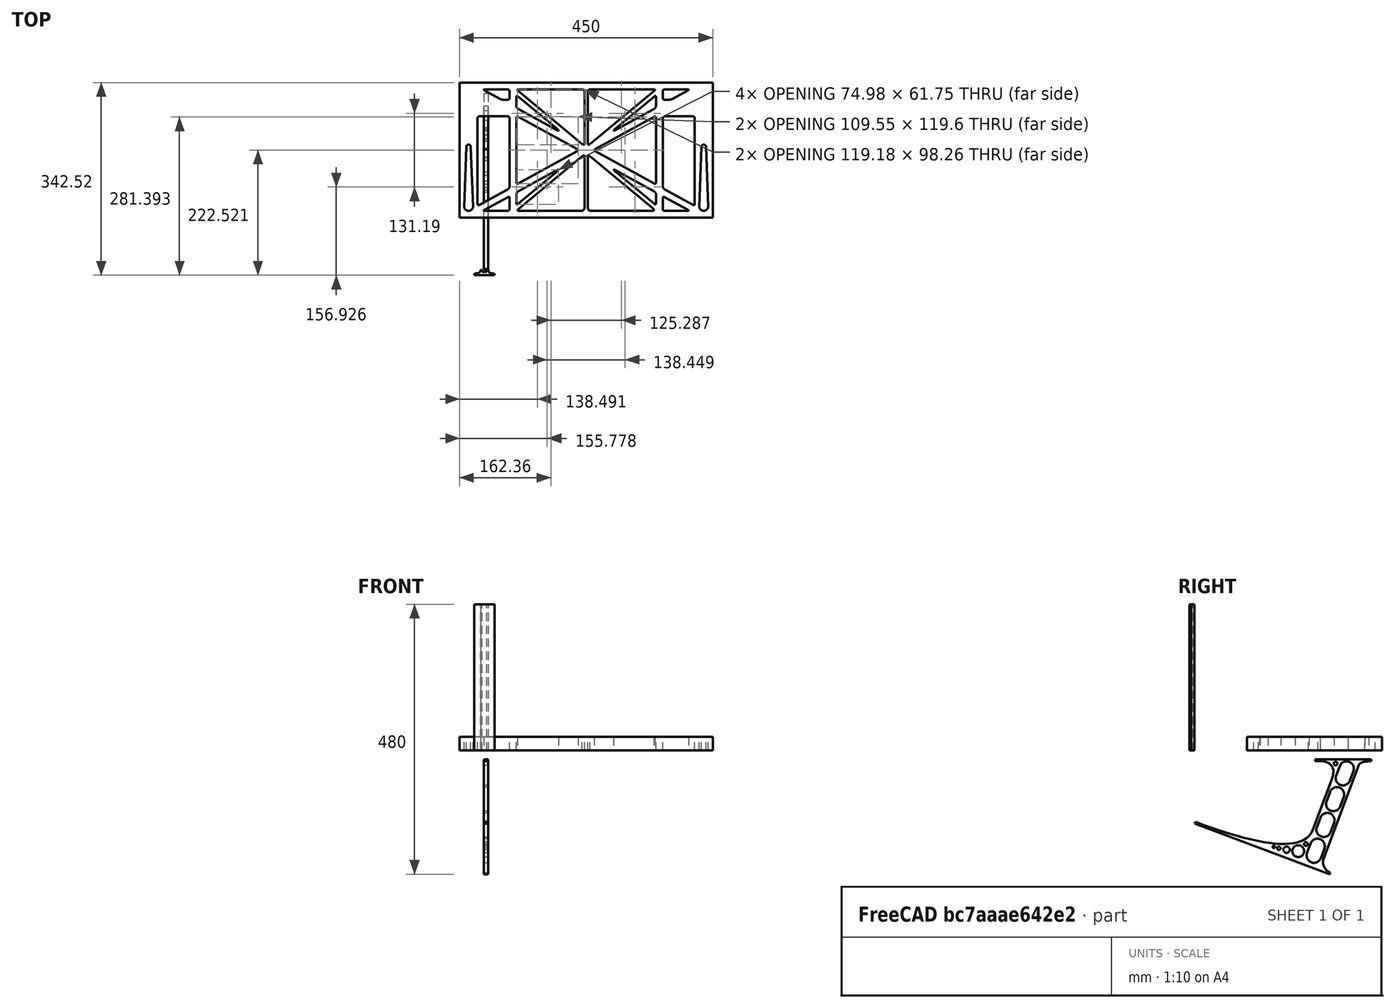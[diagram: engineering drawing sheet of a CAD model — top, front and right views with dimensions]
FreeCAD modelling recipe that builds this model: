
FCSTD DOCUMENT  (FreeCAD 0.19R0.19.2)
Label: laptopStand174FCStd
License: All rights reserved
LicenseURL: http://en.wikipedia.org/wiki/All_rights_reserved
objects: Sketcher::SketchObject×4, Part::Extrusion×3
note: 7 computed .brp shape members not serialized (recipe doc carries the construction recipe); baked Part::Feature solids carry a one-line shape summary decoded from their .brp

FEATURE [Sketcher::SketchObject] Sketch
  FullyConstrained = false
  sketch-geometry (349):
    g0: LineSegment StartX=-10.9272 StartY=-82.7794 StartZ=0 EndX=46.0728 EndY=-51.4823 EndZ=0
    g1: LineSegment StartX=-10.9272 StartY=76.4095 StartZ=0 EndX=-10.9272 EndY=-82.7794 EndZ=0
    g2: LineSegment StartX=46.0728 StartY=76.4095 StartZ=0 EndX=46.0728 EndY=-51.4823 EndZ=0
    g3: LineSegment StartX=-42.9272 StartY=136.221 StartZ=0 EndX=-42.9272 EndY=-103.779 EndZ=0
    g4: LineSegment StartX=407.073 StartY=136.221 StartZ=0 EndX=407.073 EndY=-103.779 EndZ=0
    g5: ArcOfCircle CenterX=-26.9272 CenterY=-83.7794 CenterZ=0 NormalX=0 NormalY=0 NormalZ=1 AngleXU=0 Radius=8 StartAngle=3.14159 EndAngle=6.28319
    g6: ArcOfCircle CenterX=391.073 CenterY=22.1087 CenterZ=0 NormalX=0 NormalY=0 NormalZ=1 AngleXU=0 Radius=8 StartAngle=-4.4e-15 EndAngle=3.14159
    g7: LineSegment StartX=399.073 StartY=22.1087 StartZ=0 EndX=399.073 EndY=-83.7794 EndZ=0
    g8: LineSegment StartX=383.073 StartY=22.1087 StartZ=0 EndX=383.073 EndY=-83.7794 EndZ=0
    g9: ArcOfCircle CenterX=391.073 CenterY=-83.7794 CenterZ=0 NormalX=0 NormalY=0 NormalZ=1 AngleXU=0 Radius=8 StartAngle=3.14159 EndAngle=6.28319
    g10: Circle CenterX=175.022 CenterY=27.0628 CenterZ=0 NormalX=0 NormalY=0 NormalZ=1 AngleXU=0 Radius=1
    g11: Circle CenterX=179.022 CenterY=24.8665 CenterZ=0 NormalX=0 NormalY=0 NormalZ=1 AngleXU=0 Radius=1
    g12: Circle CenterX=179.022 CenterY=27.0628 CenterZ=0 NormalX=0 NormalY=0 NormalZ=1 AngleXU=0 Radius=1
    g13: BSplineCurve PolesCount=3 KnotsCount=2 Degree=2 IsPeriodic=0
    g14: GeomPoint X=175.022 Y=27.0628 Z=0
    g15: GeomPoint X=179.022 Y=27.0628 Z=0
    g16: Circle CenterX=189.124 CenterY=27.0628 CenterZ=0 NormalX=0 NormalY=0 NormalZ=1 AngleXU=0 Radius=1
    g17: Circle CenterX=185.124 CenterY=24.8665 CenterZ=0 NormalX=0 NormalY=0 NormalZ=1 AngleXU=0 Radius=1
    g18: Circle CenterX=185.124 CenterY=27.0628 CenterZ=0 NormalX=0 NormalY=0 NormalZ=1 AngleXU=0 Radius=1
    g19: BSplineCurve PolesCount=3 KnotsCount=2 Degree=2 IsPeriodic=0
    g20: GeomPoint X=189.124 Y=27.0628 Z=0
    g21: GeomPoint X=185.124 Y=27.0628 Z=0
    g22: Circle CenterX=175.022 CenterY=5.37834 CenterZ=0 NormalX=0 NormalY=0 NormalZ=1 AngleXU=0 Radius=1
    g23: Circle CenterX=179.022 CenterY=7.57463 CenterZ=0 NormalX=0 NormalY=0 NormalZ=1 AngleXU=0 Radius=1
    g24: Circle CenterX=179.022 CenterY=5.34704 CenterZ=0 NormalX=0 NormalY=0 NormalZ=1 AngleXU=0 Radius=1
    g25: BSplineCurve PolesCount=3 KnotsCount=2 Degree=2 IsPeriodic=0
    g26: GeomPoint X=175.022 Y=5.37834 Z=0
    g27: GeomPoint X=179.022 Y=5.34704 Z=0
    g28: Circle CenterX=189.124 CenterY=5.37834 CenterZ=0 NormalX=0 NormalY=0 NormalZ=1 AngleXU=0 Radius=1
    g29: Circle CenterX=185.124 CenterY=7.57463 CenterZ=0 NormalX=0 NormalY=0 NormalZ=1 AngleXU=0 Radius=1
    g30: Circle CenterX=185.124 CenterY=5.34704 CenterZ=0 NormalX=0 NormalY=0 NormalZ=1 AngleXU=0 Radius=1
    g31: BSplineCurve PolesCount=3 KnotsCount=2 Degree=2 IsPeriodic=0
    g32: GeomPoint X=189.124 Y=5.37834 Z=0
    g33: GeomPoint X=185.124 Y=5.34704 Z=0
    g34: Circle CenterX=165.871 CenterY=18.1458 CenterZ=0 NormalX=0 NormalY=0 NormalZ=1 AngleXU=0 Radius=1
    g35: Circle CenterX=169.377 CenterY=16.2206 CenterZ=0 NormalX=0 NormalY=0 NormalZ=1 AngleXU=0 Radius=1
    g36: Circle CenterX=165.871 CenterY=14.2954 CenterZ=0 NormalX=0 NormalY=0 NormalZ=1 AngleXU=0 Radius=1
    g37: BSplineCurve PolesCount=3 KnotsCount=2 Degree=2 IsPeriodic=0
    g38: GeomPoint X=165.871 Y=18.1458 Z=0
    g39: GeomPoint X=165.871 Y=14.2954 Z=0
    g40: Circle CenterX=198.275 CenterY=18.1458 CenterZ=0 NormalX=0 NormalY=0 NormalZ=1 AngleXU=0 Radius=1
    g41: Circle CenterX=194.768 CenterY=16.2206 CenterZ=0 NormalX=0 NormalY=0 NormalZ=1 AngleXU=0 Radius=1
    g42: Circle CenterX=198.275 CenterY=14.2954 CenterZ=0 NormalX=0 NormalY=0 NormalZ=1 AngleXU=0 Radius=1
    g43: BSplineCurve PolesCount=3 KnotsCount=2 Degree=2 IsPeriodic=0
    g44: GeomPoint X=198.275 Y=18.1458 Z=0
    g45: GeomPoint X=198.275 Y=14.2954 Z=0
    g46: LineSegment StartX=407.073 StartY=-103.779 StartZ=0 EndX=-42.9272 EndY=-103.779 EndZ=0
    g47: LineSegment StartX=407.073 StartY=136.221 StartZ=0 EndX=-42.9272 EndY=136.221 EndZ=0
    g48: LineSegment StartX=46.0728 StartY=76.4095 StartZ=0 EndX=-10.9272 EndY=76.4095 EndZ=0
    g49: Circle CenterX=125.607 CenterY=54.1951 CenterZ=0 NormalX=0 NormalY=0 NormalZ=1 AngleXU=0 Radius=1
    g50: Circle CenterX=139.632 CenterY=46.4944 CenterZ=0 NormalX=0 NormalY=0 NormalZ=1 AngleXU=0 Radius=1
    g51: Circle CenterX=127.326 CenterY=56.7187 CenterZ=0 NormalX=0 NormalY=0 NormalZ=1 AngleXU=0 Radius=1
    g52: BSplineCurve PolesCount=3 KnotsCount=2 Degree=2 IsPeriodic=0
    g53: GeomPoint X=125.607 Y=54.1951 Z=0
    g54: GeomPoint X=127.326 Y=56.7187 Z=0
    g55: Circle CenterX=236.821 CenterY=56.7187 CenterZ=0 NormalX=0 NormalY=0 NormalZ=1 AngleXU=0 Radius=1
    g56: Circle CenterX=224.513 CenterY=46.4944 CenterZ=0 NormalX=0 NormalY=0 NormalZ=1 AngleXU=0 Radius=1
    g57: Circle CenterX=238.538 CenterY=54.1951 CenterZ=0 NormalX=0 NormalY=0 NormalZ=1 AngleXU=0 Radius=1
    g58: BSplineCurve PolesCount=3 KnotsCount=2 Degree=2 IsPeriodic=0
    g59: GeomPoint X=236.821 Y=56.7187 Z=0
    g60: GeomPoint X=238.538 Y=54.1951 Z=0
    g61: Circle CenterX=238.538 CenterY=-21.7539 CenterZ=0 NormalX=0 NormalY=0 NormalZ=1 AngleXU=0 Radius=1
    g62: Circle CenterX=224.513 CenterY=-14.0532 CenterZ=0 NormalX=0 NormalY=0 NormalZ=1 AngleXU=0 Radius=1
    g63: Circle CenterX=236.821 CenterY=-24.2775 CenterZ=0 NormalX=0 NormalY=0 NormalZ=1 AngleXU=0 Radius=1
    g64: BSplineCurve PolesCount=3 KnotsCount=2 Degree=2 IsPeriodic=0
    g65: GeomPoint X=238.538 Y=-21.7539 Z=0
    g66: GeomPoint X=236.821 Y=-24.2775 Z=0
    g67: Circle CenterX=125.607 CenterY=-21.7539 CenterZ=0 NormalX=0 NormalY=0 NormalZ=1 AngleXU=0 Radius=1
    g68: Circle CenterX=139.632 CenterY=-14.0532 CenterZ=0 NormalX=0 NormalY=0 NormalZ=1 AngleXU=0 Radius=1
    g69: Circle CenterX=127.325 CenterY=-24.2775 CenterZ=0 NormalX=0 NormalY=0 NormalZ=1 AngleXU=0 Radius=1
    g70: BSplineCurve PolesCount=3 KnotsCount=2 Degree=2 IsPeriodic=0
    g71: GeomPoint X=125.607 Y=-21.7539 Z=0
    g72: GeomPoint X=127.325 Y=-24.2775 Z=0
    g73: Circle CenterX=302.996 CenterY=111.695 CenterZ=0 NormalX=0 NormalY=0 NormalZ=1 AngleXU=0 Radius=1
    g74: Circle CenterX=306.073 CenterY=114.251 CenterZ=0 NormalX=0 NormalY=0 NormalZ=1 AngleXU=0 Radius=1
    g75: Circle CenterX=306.073 CenterY=110.251 CenterZ=0 NormalX=0 NormalY=0 NormalZ=1 AngleXU=0 Radius=1
    g76: BSplineCurve PolesCount=3 KnotsCount=2 Degree=2 IsPeriodic=0
    g77: GeomPoint X=302.996 Y=111.695 Z=0
    g78: GeomPoint X=306.073 Y=110.251 Z=0
    g79: Circle CenterX=306.073 CenterY=95.2763 CenterZ=0 NormalX=0 NormalY=0 NormalZ=1 AngleXU=0 Radius=1
    g80: Circle CenterX=306.073 CenterY=91.2763 CenterZ=0 NormalX=0 NormalY=0 NormalZ=1 AngleXU=0 Radius=1
    g81: Circle CenterX=302.567 CenterY=89.3511 CenterZ=0 NormalX=0 NormalY=0 NormalZ=1 AngleXU=0 Radius=1
    g82: BSplineCurve PolesCount=3 KnotsCount=2 Degree=2 IsPeriodic=0
    g83: GeomPoint X=306.073 Y=95.2763 Z=0
    g84: GeomPoint X=302.567 Y=89.3511 Z=0
    g85: LineSegment StartX=306.073 StartY=110.251 StartZ=0 EndX=306.073 EndY=95.2763 EndZ=0
    g86: LineSegment StartX=302.996 StartY=111.695 StartZ=0 EndX=236.821 EndY=56.7187 EndZ=0
    g87: LineSegment StartX=238.538 StartY=54.1951 StartZ=0 EndX=302.567 EndY=89.3511 EndZ=0
    g88: Circle CenterX=61.1496 CenterY=111.695 CenterZ=0 NormalX=0 NormalY=0 NormalZ=1 AngleXU=0 Radius=1
    g89: Circle CenterX=58.0728 CenterY=114.251 CenterZ=0 NormalX=0 NormalY=0 NormalZ=1 AngleXU=0 Radius=1
    g90: Circle CenterX=58.0728 CenterY=110.251 CenterZ=0 NormalX=0 NormalY=0 NormalZ=1 AngleXU=0 Radius=1
    g91: BSplineCurve PolesCount=3 KnotsCount=2 Degree=2 IsPeriodic=0
    g92: GeomPoint X=61.1496 Y=111.695 Z=0
    g93: GeomPoint X=58.0728 Y=110.251 Z=0
    g94: Circle CenterX=61.5791 CenterY=89.3511 CenterZ=0 NormalX=0 NormalY=0 NormalZ=1 AngleXU=0 Radius=1
    g95: Circle CenterX=58.0728 CenterY=91.2763 CenterZ=0 NormalX=0 NormalY=0 NormalZ=1 AngleXU=0 Radius=1
    g96: Circle CenterX=58.0728 CenterY=95.2763 CenterZ=0 NormalX=0 NormalY=0 NormalZ=1 AngleXU=0 Radius=1
    g97: BSplineCurve PolesCount=3 KnotsCount=2 Degree=2 IsPeriodic=0
    g98: GeomPoint X=61.5791 Y=89.3511 Z=0
    g99: GeomPoint X=58.0728 Y=95.2763 Z=0
    g100: LineSegment StartX=58.0728 StartY=110.251 StartZ=0 EndX=58.0728 EndY=95.2763 EndZ=0
    g101: LineSegment StartX=61.1496 StartY=111.695 StartZ=0 EndX=127.326 EndY=56.7187 EndZ=0
    g102: LineSegment StartX=125.607 StartY=54.1951 StartZ=0 EndX=61.5791 EndY=89.3511 EndZ=0
    g103: Circle CenterX=61.5791 CenterY=-56.9099 CenterZ=0 NormalX=0 NormalY=0 NormalZ=1 AngleXU=0 Radius=1
    g104: Circle CenterX=58.0728 CenterY=-58.8351 CenterZ=0 NormalX=0 NormalY=0 NormalZ=1 AngleXU=0 Radius=1
    g105: Circle CenterX=58.0728 CenterY=-62.8351 CenterZ=0 NormalX=0 NormalY=0 NormalZ=1 AngleXU=0 Radius=1
    g106: BSplineCurve PolesCount=3 KnotsCount=2 Degree=2 IsPeriodic=0
    g107: GeomPoint X=61.5791 Y=-56.9099 Z=0
    g108: GeomPoint X=58.0728 Y=-62.8351 Z=0
    g109: Circle CenterX=58.0728 CenterY=-77.8102 CenterZ=0 NormalX=0 NormalY=0 NormalZ=1 AngleXU=0 Radius=1
    g110: Circle CenterX=58.0728 CenterY=-81.8102 CenterZ=0 NormalX=0 NormalY=0 NormalZ=1 AngleXU=0 Radius=1
    g111: Circle CenterX=61.1496 CenterY=-79.2541 CenterZ=0 NormalX=0 NormalY=0 NormalZ=1 AngleXU=0 Radius=1
    g112: BSplineCurve PolesCount=3 KnotsCount=2 Degree=2 IsPeriodic=0
    g113: GeomPoint X=58.0728 Y=-77.8102 Z=0
    g114: GeomPoint X=61.1496 Y=-79.2541 Z=0
    g115: LineSegment StartX=58.0728 StartY=-62.8351 StartZ=0 EndX=58.0728 EndY=-77.8102 EndZ=0
    g116: LineSegment StartX=61.1496 StartY=-79.2541 StartZ=0 EndX=127.325 EndY=-24.2775 EndZ=0
    g117: LineSegment StartX=125.607 StartY=-21.7539 StartZ=0 EndX=61.5791 EndY=-56.9099 EndZ=0
    g118: Circle CenterX=302.567 CenterY=-56.9099 CenterZ=0 NormalX=0 NormalY=0 NormalZ=1 AngleXU=0 Radius=1
    g119: Circle CenterX=306.073 CenterY=-58.8351 CenterZ=0 NormalX=0 NormalY=0 NormalZ=1 AngleXU=0 Radius=1
    g120: Circle CenterX=306.073 CenterY=-62.8351 CenterZ=0 NormalX=0 NormalY=0 NormalZ=1 AngleXU=0 Radius=1
    g121: BSplineCurve PolesCount=3 KnotsCount=2 Degree=2 IsPeriodic=0
    g122: GeomPoint X=302.567 Y=-56.9099 Z=0
    g123: GeomPoint X=306.073 Y=-62.8351 Z=0
    g124: Circle CenterX=302.996 CenterY=-79.2541 CenterZ=0 NormalX=0 NormalY=0 NormalZ=1 AngleXU=0 Radius=1
    g125: Circle CenterX=306.073 CenterY=-81.8102 CenterZ=0 NormalX=0 NormalY=0 NormalZ=1 AngleXU=0 Radius=1
    g126: Circle CenterX=306.073 CenterY=-77.8102 CenterZ=0 NormalX=0 NormalY=0 NormalZ=1 AngleXU=0 Radius=1
    g127: BSplineCurve PolesCount=3 KnotsCount=2 Degree=2 IsPeriodic=0
    g128: GeomPoint X=302.996 Y=-79.2541 Z=0
    g129: GeomPoint X=306.073 Y=-77.8102 Z=0
    g130: LineSegment StartX=306.073 StartY=-62.8351 StartZ=0 EndX=306.073 EndY=-77.8102 EndZ=0
    g131: LineSegment StartX=302.996 StartY=-79.2541 StartZ=0 EndX=236.821 EndY=-24.2775 EndZ=0
    g132: LineSegment StartX=238.538 StartY=-21.7539 StartZ=0 EndX=302.567 EndY=-56.9099 EndZ=0
    g133: Circle CenterX=61.6457 CenterY=-88.8112 CenterZ=0 NormalX=0 NormalY=0 NormalZ=1 AngleXU=0 Radius=1
    g134: Circle CenterX=58.0728 CenterY=-91.7794 CenterZ=0 NormalX=0 NormalY=0 NormalZ=1 AngleXU=0 Radius=1
    g135: Circle CenterX=63.9135 CenterY=-91.7794 CenterZ=0 NormalX=0 NormalY=0 NormalZ=1 AngleXU=0 Radius=1
    g136: BSplineCurve PolesCount=3 KnotsCount=2 Degree=2 IsPeriodic=0
    g137: GeomPoint X=61.6457 Y=-88.8112 Z=0
    g138: GeomPoint X=63.9135 Y=-91.7794 Z=0
    g139: Circle CenterX=179.022 CenterY=-85.8163 CenterZ=0 NormalX=0 NormalY=0 NormalZ=1 AngleXU=0 Radius=1
    g140: Circle CenterX=179.022 CenterY=-91.7794 CenterZ=0 NormalX=0 NormalY=0 NormalZ=1 AngleXU=0 Radius=1
    g141: Circle CenterX=171.895 CenterY=-91.7794 CenterZ=0 NormalX=0 NormalY=0 NormalZ=1 AngleXU=0 Radius=1
    g142: BSplineCurve PolesCount=3 KnotsCount=2 Degree=2 IsPeriodic=0
    g143: GeomPoint X=179.022 Y=-85.8163 Z=0
    g144: GeomPoint X=171.895 Y=-91.7794 Z=0
    g145: Circle CenterX=185.124 CenterY=-86.2028 CenterZ=0 NormalX=0 NormalY=0 NormalZ=1 AngleXU=0 Radius=1
    g146: Circle CenterX=185.124 CenterY=-91.7794 CenterZ=0 NormalX=0 NormalY=0 NormalZ=1 AngleXU=0 Radius=1
    g147: Circle CenterX=191.747 CenterY=-91.7794 CenterZ=0 NormalX=0 NormalY=0 NormalZ=1 AngleXU=0 Radius=1
    g148: BSplineCurve PolesCount=3 KnotsCount=2 Degree=2 IsPeriodic=0
    g149: GeomPoint X=185.124 Y=-86.2028 Z=0
    g150: GeomPoint X=191.747 Y=-91.7794 Z=0
    g151: Circle CenterX=299.888 CenterY=-86.6413 CenterZ=0 NormalX=0 NormalY=0 NormalZ=1 AngleXU=0 Radius=1
    g152: Circle CenterX=306.073 CenterY=-91.7794 CenterZ=0 NormalX=0 NormalY=0 NormalZ=1 AngleXU=0 Radius=1
    g153: Circle CenterX=298.776 CenterY=-91.7794 CenterZ=0 NormalX=0 NormalY=0 NormalZ=1 AngleXU=0 Radius=1
    g154: BSplineCurve PolesCount=3 KnotsCount=2 Degree=2 IsPeriodic=0
    g155: GeomPoint X=299.888 Y=-86.6413 Z=0
    g156: GeomPoint X=298.776 Y=-91.7794 Z=0
    g157: LineSegment StartX=189.124 StartY=5.37834 StartZ=0 EndX=299.888 EndY=-86.6413 EndZ=0
    g158: LineSegment StartX=298.776 StartY=-91.7794 StartZ=0 EndX=191.747 EndY=-91.7794 EndZ=0
    g159: LineSegment StartX=185.124 StartY=-86.2028 StartZ=0 EndX=185.124 EndY=5.34704 EndZ=0
    g160: LineSegment StartX=179.022 StartY=5.34704 StartZ=0 EndX=179.022 EndY=-85.8163 EndZ=0
    g161: LineSegment StartX=171.895 StartY=-91.7794 StartZ=0 EndX=63.9135 EndY=-91.7794 EndZ=0
    g162: LineSegment StartX=61.6457 StartY=-88.8112 StartZ=0 EndX=175.022 EndY=5.37834 EndZ=0
    g163: Circle CenterX=302.073 CenterY=124.221 CenterZ=0 NormalX=0 NormalY=0 NormalZ=1 AngleXU=0 Radius=1
    g164: Circle CenterX=306.073 CenterY=124.221 CenterZ=0 NormalX=0 NormalY=0 NormalZ=1 AngleXU=0 Radius=1
    g165: Circle CenterX=302.996 CenterY=121.665 CenterZ=0 NormalX=0 NormalY=0 NormalZ=1 AngleXU=0 Radius=1
    g166: BSplineCurve PolesCount=3 KnotsCount=2 Degree=2 IsPeriodic=0
    g167: GeomPoint X=302.073 Y=124.221 Z=0
    g168: GeomPoint X=302.996 Y=121.665 Z=0
    g169: Circle CenterX=189.124 CenterY=124.221 CenterZ=0 NormalX=0 NormalY=0 NormalZ=1 AngleXU=0 Radius=1
    g170: Circle CenterX=185.124 CenterY=124.221 CenterZ=0 NormalX=0 NormalY=0 NormalZ=1 AngleXU=0 Radius=1
    g171: Circle CenterX=185.124 CenterY=120.221 CenterZ=0 NormalX=0 NormalY=0 NormalZ=1 AngleXU=0 Radius=1
    g172: BSplineCurve PolesCount=3 KnotsCount=2 Degree=2 IsPeriodic=0
    g173: GeomPoint X=189.124 Y=124.221 Z=0
    g174: GeomPoint X=185.124 Y=120.221 Z=0
    g175: Circle CenterX=175.022 CenterY=124.221 CenterZ=0 NormalX=0 NormalY=0 NormalZ=1 AngleXU=0 Radius=1
    g176: Circle CenterX=179.022 CenterY=124.221 CenterZ=0 NormalX=0 NormalY=0 NormalZ=1 AngleXU=0 Radius=1
    g177: Circle CenterX=179.022 CenterY=120.221 CenterZ=0 NormalX=0 NormalY=0 NormalZ=1 AngleXU=0 Radius=1
    g178: BSplineCurve PolesCount=3 KnotsCount=2 Degree=2 IsPeriodic=0
    g179: GeomPoint X=175.022 Y=124.221 Z=0
    g180: GeomPoint X=179.022 Y=120.221 Z=0
    g181: Circle CenterX=62.0728 CenterY=124.221 CenterZ=0 NormalX=0 NormalY=0 NormalZ=1 AngleXU=0 Radius=1
    g182: Circle CenterX=58.0728 CenterY=124.221 CenterZ=0 NormalX=0 NormalY=0 NormalZ=1 AngleXU=0 Radius=1
    g183: Circle CenterX=61.1496 CenterY=121.665 CenterZ=0 NormalX=0 NormalY=0 NormalZ=1 AngleXU=0 Radius=1
    g184: BSplineCurve PolesCount=3 KnotsCount=2 Degree=2 IsPeriodic=0
    g185: GeomPoint X=62.0728 Y=124.221 Z=0
    g186: GeomPoint X=61.1496 Y=121.665 Z=0
    g187: LineSegment StartX=62.0728 StartY=124.221 StartZ=0 EndX=175.022 EndY=124.221 EndZ=0
    g188: LineSegment StartX=179.022 StartY=120.221 StartZ=0 EndX=179.022 EndY=27.0628 EndZ=0
    g189: LineSegment StartX=185.124 StartY=27.0628 StartZ=0 EndX=185.124 EndY=120.221 EndZ=0
    g190: LineSegment StartX=189.124 StartY=124.221 StartZ=0 EndX=302.073 EndY=124.221 EndZ=0
    g191: LineSegment StartX=302.996 StartY=121.665 StartZ=0 EndX=189.124 EndY=27.0628 EndZ=0
    g192: LineSegment StartX=175.022 StartY=27.0628 StartZ=0 EndX=61.1496 EndY=121.665 EndZ=0
    g193: Circle CenterX=61.5791 CenterY=75.4095 CenterZ=0 NormalX=0 NormalY=0 NormalZ=1 AngleXU=0 Radius=1
    g194: Circle CenterX=58.0728 CenterY=77.3346 CenterZ=0 NormalX=0 NormalY=0 NormalZ=1 AngleXU=0 Radius=1
    g195: Circle CenterX=58.0728 CenterY=73.3346 CenterZ=0 NormalX=0 NormalY=0 NormalZ=1 AngleXU=0 Radius=1
    g196: BSplineCurve PolesCount=3 KnotsCount=2 Degree=2 IsPeriodic=0
    g197: GeomPoint X=61.5791 Y=75.4095 Z=0
    g198: GeomPoint X=58.0728 Y=73.3346 Z=0
    g199: Circle CenterX=58.0728 CenterY=-40.8935 CenterZ=0 NormalX=0 NormalY=0 NormalZ=1 AngleXU=0 Radius=1
    g200: Circle CenterX=58.0728 CenterY=-44.8935 CenterZ=0 NormalX=0 NormalY=0 NormalZ=1 AngleXU=0 Radius=1
    g201: Circle CenterX=61.5791 CenterY=-42.9683 CenterZ=0 NormalX=0 NormalY=0 NormalZ=1 AngleXU=0 Radius=1
    g202: BSplineCurve PolesCount=3 KnotsCount=2 Degree=2 IsPeriodic=0
    g203: GeomPoint X=58.0728 Y=-40.8935 Z=0
    g204: GeomPoint X=61.5791 Y=-42.9683 Z=0
    g205: LineSegment StartX=61.5791 StartY=-42.9683 StartZ=0 EndX=165.871 EndY=14.2954 EndZ=0
    g206: LineSegment StartX=165.871 StartY=18.1458 StartZ=0 EndX=61.5791 EndY=75.4095 EndZ=0
    g207: LineSegment StartX=58.0728 StartY=73.3346 StartZ=0 EndX=58.0728 EndY=-40.8935 EndZ=0
    g208: Circle CenterX=302.567 CenterY=-42.9683 CenterZ=0 NormalX=0 NormalY=0 NormalZ=1 AngleXU=0 Radius=1
    g209: Circle CenterX=306.073 CenterY=-44.8935 CenterZ=0 NormalX=0 NormalY=0 NormalZ=1 AngleXU=0 Radius=1
    g210: Circle CenterX=306.073 CenterY=-40.8935 CenterZ=0 NormalX=0 NormalY=0 NormalZ=1 AngleXU=0 Radius=1
    g211: BSplineCurve PolesCount=3 KnotsCount=2 Degree=2 IsPeriodic=0
    g212: GeomPoint X=302.567 Y=-42.9683 Z=0
    g213: GeomPoint X=306.073 Y=-40.8935 Z=0
    g214: Circle CenterX=306.073 CenterY=73.3346 CenterZ=0 NormalX=0 NormalY=0 NormalZ=1 AngleXU=0 Radius=1
    g215: Circle CenterX=306.073 CenterY=77.3346 CenterZ=0 NormalX=0 NormalY=0 NormalZ=1 AngleXU=0 Radius=1
    g216: Circle CenterX=302.567 CenterY=75.4095 CenterZ=0 NormalX=0 NormalY=0 NormalZ=1 AngleXU=0 Radius=1
    g217: BSplineCurve PolesCount=3 KnotsCount=2 Degree=2 IsPeriodic=0
    g218: GeomPoint X=306.073 Y=73.3346 Z=0
    g219: GeomPoint X=302.567 Y=75.4095 Z=0
    g220: LineSegment StartX=302.567 StartY=-42.9683 StartZ=0 EndX=198.275 EndY=14.2954 EndZ=0
    g221: LineSegment StartX=198.275 StartY=18.1458 StartZ=0 EndX=302.567 EndY=75.4095 EndZ=0
    g222: LineSegment StartX=306.073 StartY=73.3346 StartZ=0 EndX=306.073 EndY=-40.8935 EndZ=0
    g223: LineSegment StartX=322.073 StartY=105.865 StartZ=0 EndX=328.643 EndY=105.865 EndZ=0
    g224: LineSegment StartX=318.073 StartY=120.221 StartZ=0 EndX=318.073 EndY=109.865 EndZ=0
    g225: LineSegment StartX=336.157 StartY=107.779 StartZ=0 EndX=362.567 EndY=122.294 EndZ=0
    g226: Circle CenterX=362.073 CenterY=124.221 CenterZ=0 NormalX=0 NormalY=0 NormalZ=1 AngleXU=0 Radius=1
    g227: Circle CenterX=366.073 CenterY=124.221 CenterZ=0 NormalX=0 NormalY=0 NormalZ=1 AngleXU=0 Radius=1
    g228: Circle CenterX=362.567 CenterY=122.294 CenterZ=0 NormalX=0 NormalY=0 NormalZ=1 AngleXU=0 Radius=1
    g229: BSplineCurve PolesCount=3 KnotsCount=2 Degree=2 IsPeriodic=0
    g230: GeomPoint X=362.073 Y=124.221 Z=0
    g231: GeomPoint X=362.567 Y=122.294 Z=0
    g232: Circle CenterX=322.073 CenterY=124.221 CenterZ=0 NormalX=0 NormalY=0 NormalZ=1 AngleXU=0 Radius=1
    g233: Circle CenterX=318.073 CenterY=124.221 CenterZ=0 NormalX=0 NormalY=0 NormalZ=1 AngleXU=0 Radius=1
    g234: Circle CenterX=318.073 CenterY=120.221 CenterZ=0 NormalX=0 NormalY=0 NormalZ=1 AngleXU=0 Radius=1
    g235: BSplineCurve PolesCount=3 KnotsCount=2 Degree=2 IsPeriodic=0
    g236: GeomPoint X=322.073 Y=124.221 Z=0
    g237: GeomPoint X=318.073 Y=120.221 Z=0
    g238: Circle CenterX=322.073 CenterY=105.865 CenterZ=0 NormalX=0 NormalY=0 NormalZ=1 AngleXU=0 Radius=1
    g239: Circle CenterX=318.073 CenterY=105.865 CenterZ=0 NormalX=0 NormalY=0 NormalZ=1 AngleXU=0 Radius=1
    g240: Circle CenterX=318.073 CenterY=109.865 CenterZ=0 NormalX=0 NormalY=0 NormalZ=1 AngleXU=0 Radius=1
    g241: BSplineCurve PolesCount=3 KnotsCount=2 Degree=2 IsPeriodic=0
    g242: GeomPoint X=322.073 Y=105.865 Z=0
    g243: GeomPoint X=318.073 Y=109.865 Z=0
    g244: Circle CenterX=336.157 CenterY=107.779 CenterZ=0 NormalX=0 NormalY=0 NormalZ=1 AngleXU=0 Radius=1
    g245: Circle CenterX=332.651 CenterY=105.853 CenterZ=0 NormalX=0 NormalY=0 NormalZ=1 AngleXU=0 Radius=1
    g246: Circle CenterX=328.643 CenterY=105.865 CenterZ=0 NormalX=0 NormalY=0 NormalZ=1 AngleXU=0 Radius=1
    g247: BSplineCurve PolesCount=3 KnotsCount=2 Degree=2 IsPeriodic=0
    g248: GeomPoint X=336.157 Y=107.779 Z=0
    g249: GeomPoint X=328.643 Y=105.865 Z=0
    g250: LineSegment StartX=322.073 StartY=124.221 StartZ=0 EndX=362.073 EndY=124.221 EndZ=0
    g251: Circle CenterX=371.567 CenterY=-80.8644 CenterZ=0 NormalX=0 NormalY=0 NormalZ=1 AngleXU=0 Radius=1
    g252: Circle CenterX=375.073 CenterY=-82.7896 CenterZ=0 NormalX=0 NormalY=0 NormalZ=1 AngleXU=0 Radius=1
    g253: Circle CenterX=375.073 CenterY=-78.7896 CenterZ=0 NormalX=0 NormalY=0 NormalZ=1 AngleXU=0 Radius=1
    g254: BSplineCurve PolesCount=3 KnotsCount=2 Degree=2 IsPeriodic=0
    g255: GeomPoint X=371.567 Y=-80.8644 Z=0
    g256: GeomPoint X=375.073 Y=-78.7896 Z=0
    g257: Circle CenterX=321.579 CenterY=-53.4075 CenterZ=0 NormalX=0 NormalY=0 NormalZ=1 AngleXU=0 Radius=1
    g258: Circle CenterX=318.073 CenterY=-51.4823 CenterZ=0 NormalX=0 NormalY=0 NormalZ=1 AngleXU=0 Radius=1
    g259: Circle CenterX=318.073 CenterY=-47.4805 CenterZ=0 NormalX=0 NormalY=0 NormalZ=1 AngleXU=0 Radius=1
    g260: BSplineCurve PolesCount=3 KnotsCount=2 Degree=2 IsPeriodic=0
    g261: GeomPoint X=321.579 Y=-53.4075 Z=0
    g262: GeomPoint X=318.073 Y=-47.4805 Z=0
    g263: LineSegment StartX=371.567 StartY=-80.8644 StartZ=0 EndX=321.579 EndY=-53.4075 EndZ=0
    g264: Circle CenterX=321.579 CenterY=-67.3492 CenterZ=0 NormalX=0 NormalY=0 NormalZ=1 AngleXU=0 Radius=1
    g265: Circle CenterX=318.073 CenterY=-65.424 CenterZ=0 NormalX=0 NormalY=0 NormalZ=1 AngleXU=0 Radius=1
    g266: Circle CenterX=318.073 CenterY=-69.424 CenterZ=0 NormalX=0 NormalY=0 NormalZ=1 AngleXU=0 Radius=1
    g267: BSplineCurve PolesCount=3 KnotsCount=2 Degree=2 IsPeriodic=0
    g268: GeomPoint X=321.579 Y=-67.3492 Z=0
    g269: GeomPoint X=318.073 Y=-69.424 Z=0
    g270: Circle CenterX=362.567 CenterY=-89.8542 CenterZ=0 NormalX=0 NormalY=0 NormalZ=1 AngleXU=0 Radius=1
    g271: Circle CenterX=366.073 CenterY=-91.7794 CenterZ=0 NormalX=0 NormalY=0 NormalZ=1 AngleXU=0 Radius=1
    g272: Circle CenterX=362.073 CenterY=-91.7794 CenterZ=0 NormalX=0 NormalY=0 NormalZ=1 AngleXU=0 Radius=1
    g273: BSplineCurve PolesCount=3 KnotsCount=2 Degree=2 IsPeriodic=0
    g274: GeomPoint X=362.567 Y=-89.8542 Z=0
    g275: GeomPoint X=362.073 Y=-91.7794 Z=0
    g276: Circle CenterX=322.073 CenterY=-91.7794 CenterZ=0 NormalX=0 NormalY=0 NormalZ=1 AngleXU=0 Radius=1
    g277: Circle CenterX=318.073 CenterY=-91.7794 CenterZ=0 NormalX=0 NormalY=0 NormalZ=1 AngleXU=0 Radius=1
    g278: Circle CenterX=318.073 CenterY=-87.7794 CenterZ=0 NormalX=0 NormalY=0 NormalZ=1 AngleXU=0 Radius=1
    g279: BSplineCurve PolesCount=3 KnotsCount=2 Degree=2 IsPeriodic=0
    g280: GeomPoint X=322.073 Y=-91.7794 Z=0
    g281: GeomPoint X=318.073 Y=-87.7794 Z=0
    g282: LineSegment StartX=362.567 StartY=-89.8542 StartZ=0 EndX=321.579 EndY=-67.3492 EndZ=0
    g283: LineSegment StartX=318.073 StartY=-69.424 StartZ=0 EndX=318.073 EndY=-87.7794 EndZ=0
    g284: LineSegment StartX=322.073 StartY=-91.7794 StartZ=0 EndX=362.073 EndY=-91.7794 EndZ=0
    g285: Circle CenterX=2.07281 CenterY=124.221 CenterZ=0 NormalX=0 NormalY=0 NormalZ=1 AngleXU=0 Radius=1
    g286: Circle CenterX=1.57905 CenterY=122.295 CenterZ=0 NormalX=0 NormalY=0 NormalZ=1 AngleXU=0 Radius=1
    g287: BSplineCurve PolesCount=3 KnotsCount=2 Degree=2 IsPeriodic=0
    g288: GeomPoint X=2.07281 Y=124.221 Z=0
    g289: GeomPoint X=1.57905 Y=122.295 Z=0
    g290: Circle CenterX=42.0728 CenterY=124.221 CenterZ=0 NormalX=0 NormalY=0 NormalZ=1 AngleXU=0 Radius=1
    g291: Circle CenterX=46.0728 CenterY=124.221 CenterZ=0 NormalX=0 NormalY=0 NormalZ=1 AngleXU=0 Radius=1
    g292: Circle CenterX=46.0728 CenterY=120.221 CenterZ=0 NormalX=0 NormalY=0 NormalZ=1 AngleXU=0 Radius=1
    g293: BSplineCurve PolesCount=3 KnotsCount=2 Degree=2 IsPeriodic=0
    g294: GeomPoint X=42.0728 Y=124.221 Z=0
    g295: GeomPoint X=46.0728 Y=120.221 Z=0
    g296: Circle CenterX=46.0728 CenterY=109.865 CenterZ=0 NormalX=0 NormalY=0 NormalZ=1 AngleXU=0 Radius=1
    g297: Circle CenterX=46.0728 CenterY=105.865 CenterZ=0 NormalX=0 NormalY=0 NormalZ=1 AngleXU=0 Radius=1
    g298: Circle CenterX=42.0728 CenterY=105.865 CenterZ=0 NormalX=0 NormalY=0 NormalZ=1 AngleXU=0 Radius=1
    g299: BSplineCurve PolesCount=3 KnotsCount=2 Degree=2 IsPeriodic=0
    g300: GeomPoint X=46.0728 Y=109.865 Z=0
    g301: GeomPoint X=42.0728 Y=105.865 Z=0
    g302: Circle CenterX=35.5028 CenterY=105.865 CenterZ=0 NormalX=0 NormalY=0 NormalZ=1 AngleXU=0 Radius=1
    g303: Circle CenterX=31.5028 CenterY=105.865 CenterZ=0 NormalX=0 NormalY=0 NormalZ=1 AngleXU=0 Radius=1
    g304: Circle CenterX=27.9965 CenterY=107.79 CenterZ=0 NormalX=0 NormalY=0 NormalZ=1 AngleXU=0 Radius=1
    g305: BSplineCurve PolesCount=3 KnotsCount=2 Degree=2 IsPeriodic=0
    g306: GeomPoint X=35.5028 Y=105.865 Z=0
    g307: GeomPoint X=27.9965 Y=107.79 Z=0
    g308: LineSegment StartX=2.07281 StartY=124.221 StartZ=0 EndX=42.0728 EndY=124.221 EndZ=0
    g309: LineSegment StartX=46.0728 StartY=120.221 StartZ=0 EndX=46.0728 EndY=109.865 EndZ=0
    g310: LineSegment StartX=42.0728 StartY=105.865 StartZ=0 EndX=35.5028 EndY=105.865 EndZ=0
    g311: LineSegment StartX=27.9965 StartY=107.79 StartZ=0 EndX=1.57905 EndY=122.295 EndZ=0
    g312: Circle CenterX=42.5666 CenterY=-67.3492 CenterZ=0 NormalX=0 NormalY=0 NormalZ=1 AngleXU=0 Radius=1
    g313: Circle CenterX=46.0728 CenterY=-65.424 CenterZ=0 NormalX=0 NormalY=0 NormalZ=1 AngleXU=0 Radius=1
    g314: Circle CenterX=46.0728 CenterY=-69.424 CenterZ=0 NormalX=0 NormalY=0 NormalZ=1 AngleXU=0 Radius=1
    g315: BSplineCurve PolesCount=3 KnotsCount=2 Degree=2 IsPeriodic=0
    g316: GeomPoint X=42.5666 Y=-67.3492 Z=0
    g317: GeomPoint X=46.0728 Y=-69.424 Z=0
    g318: Circle CenterX=46.0728 CenterY=-87.7794 CenterZ=0 NormalX=0 NormalY=0 NormalZ=1 AngleXU=0 Radius=1
    g319: Circle CenterX=46.0728 CenterY=-91.7794 CenterZ=0 NormalX=0 NormalY=0 NormalZ=1 AngleXU=0 Radius=1
    g320: Circle CenterX=42.0728 CenterY=-91.7794 CenterZ=0 NormalX=0 NormalY=0 NormalZ=1 AngleXU=0 Radius=1
    g321: BSplineCurve PolesCount=3 KnotsCount=2 Degree=2 IsPeriodic=0
    g322: GeomPoint X=46.0728 Y=-87.7794 Z=0
    g323: GeomPoint X=42.0728 Y=-91.7794 Z=0
    g324: Circle CenterX=2.07281 CenterY=-91.7794 CenterZ=0 NormalX=0 NormalY=0 NormalZ=1 AngleXU=0 Radius=1
    g325: Circle CenterX=-1.92719 CenterY=-91.7794 CenterZ=0 NormalX=0 NormalY=0 NormalZ=1 AngleXU=0 Radius=1
    g326: Circle CenterX=1.57905 CenterY=-89.8542 CenterZ=0 NormalX=0 NormalY=0 NormalZ=1 AngleXU=0 Radius=1
    g327: BSplineCurve PolesCount=3 KnotsCount=2 Degree=2 IsPeriodic=0
    g328: GeomPoint X=2.07281 Y=-91.7794 Z=0
    g329: GeomPoint X=1.57905 Y=-89.8542 Z=0
    g330: LineSegment StartX=2.07281 StartY=-91.7794 StartZ=0 EndX=42.0728 EndY=-91.7794 EndZ=0
    g331: LineSegment StartX=46.0728 StartY=-87.7794 StartZ=0 EndX=46.0728 EndY=-69.424 EndZ=0
    g332: LineSegment StartX=42.5666 StartY=-67.3492 StartZ=0 EndX=1.57905 EndY=-89.8542 EndZ=0
    g333: Circle CenterX=322.073 CenterY=76.4095 CenterZ=0 NormalX=0 NormalY=0 NormalZ=1 AngleXU=0 Radius=4
    g334: BSplineCurve PolesCount=3 KnotsCount=2 Degree=2 IsPeriodic=0
    g335: GeomPoint X=318.073 Y=72.4095 Z=0
    g336: GeomPoint X=322.073 Y=76.4095 Z=0
    g337: Circle CenterX=375.073 CenterY=72.4095 CenterZ=0 NormalX=0 NormalY=0 NormalZ=1 AngleXU=0 Radius=1
    g338: Circle CenterX=375.073 CenterY=76.4095 CenterZ=0 NormalX=0 NormalY=0 NormalZ=1 AngleXU=0 Radius=1
    g339: Circle CenterX=371.073 CenterY=76.4095 CenterZ=0 NormalX=0 NormalY=0 NormalZ=1 AngleXU=0 Radius=1
    g340: BSplineCurve PolesCount=3 KnotsCount=2 Degree=2 IsPeriodic=0
    g341: GeomPoint X=375.073 Y=72.4095 Z=0
    g342: GeomPoint X=371.073 Y=76.4095 Z=0
    g343: LineSegment StartX=322.073 StartY=76.4095 StartZ=0 EndX=371.073 EndY=76.4095 EndZ=0
    g344: LineSegment StartX=318.073 StartY=72.4095 StartZ=0 EndX=318.073 EndY=-47.4805 EndZ=0
    g345: LineSegment StartX=375.073 StartY=72.4095 StartZ=0 EndX=375.073 EndY=-78.7896 EndZ=0
    g346: ArcOfCircle CenterX=-26.9272 CenterY=22.1087 CenterZ=0 NormalX=0 NormalY=0 NormalZ=1 AngleXU=0 Radius=4 StartAngle=5e-16 EndAngle=3.14159
    g347: LineSegment StartX=-30.9272 StartY=22.1087 StartZ=0 EndX=-34.9272 EndY=-83.7794 EndZ=0
    g348: LineSegment StartX=-18.9272 StartY=-83.7794 StartZ=0 EndX=-22.9272 EndY=22.1087 EndZ=0
  constraints (572):
    c: Coincident(g0,g2)
    c: Block(g0)
    c: Block(g1)
    c: Vertical(g3)
    c: Vertical(g4)
    c: Block(g4)
    c: Block(g3)
    c: Tangent(g6,g7) = 1.5708
    c: Tangent(g7,g9) = 1.5708
    c: Equal(g6,g9)
    c: Coincident(g8,g6)
    c: Coincident(g8,g9)
    c: Block(g7)
    c: Block(g8)
    c: Weight(g10) = 1
    c: Equal(g10,g11)
    c: Equal(g10,g12)
    c: InternalAlignment(g10,g13)
    c: InternalAlignment(g11,g13)
    c: InternalAlignment(g12,g13)
    c: InternalAlignment(g14,g13)
    c: InternalAlignment(g15,g13)
    c: Weight(g16) = 1
    c: Equal(g16,g17)
    c: Equal(g16,g18)
    c: InternalAlignment(g16,g19)
    c: InternalAlignment(g17,g19)
    c: InternalAlignment(g18,g19)
    c: InternalAlignment(g20,g19)
    c: InternalAlignment(g21,g19)
    c: Block(g19)
    c: Block(g13)
    c: Weight(g22) = 1
    c: Equal(g22,g23)
    c: Equal(g22,g24)
    c: InternalAlignment(g22,g25)
    c: InternalAlignment(g23,g25)
    c: InternalAlignment(g24,g25)
    c: InternalAlignment(g26,g25)
    c: InternalAlignment(g27,g25)
    c: Weight(g28) = 1
    c: Equal(g28,g29)
    c: Equal(g28,g30)
    c: InternalAlignment(g28,g31)
    c: InternalAlignment(g29,g31)
    c: InternalAlignment(g30,g31)
    c: InternalAlignment(g32,g31)
    c: InternalAlignment(g33,g31)
    c: Block(g31)
    c: Block(g25)
    c: Weight(g34) = 1
    c: Equal(g34,g35)
    c: Equal(g34,g36)
    c: InternalAlignment(g34,g37)
    c: InternalAlignment(g35,g37)
    c: InternalAlignment(g36,g37)
    c: InternalAlignment(g38,g37)
    c: InternalAlignment(g39,g37)
    c: Weight(g40) = 1
    c: Equal(g40,g41)
    c: Equal(g40,g42)
    c: InternalAlignment(g40,g43)
    c: InternalAlignment(g41,g43)
    c: InternalAlignment(g42,g43)
    c: InternalAlignment(g44,g43)
    c: InternalAlignment(g45,g43)
    c: Block(g37)
    c: Block(g43)
    c: Coincident(g46,g4)
    c: Coincident(g46,g3)
    c: Horizontal(g46)
    c: Distance(g46) = 450
    c: Coincident(g47,g4)
    c: Coincident(g47,g3)
    c: Horizontal(g47)
    c: Horizontal(g48)
    c: Coincident(g2,g48)
    c: Block(g48)
    c: Coincident(g1,g48)
    c: Weight(g49) = 1
    c: Equal(g49,g50)
    c: Equal(g49,g51)
    c: InternalAlignment(g49,g52)
    c: InternalAlignment(g50,g52)
    c: InternalAlignment(g51,g52)
    c: InternalAlignment(g53,g52)
    c: InternalAlignment(g54,g52)
    c: Block(g52)
    c: Weight(g55) = 1
    c: Equal(g55,g56)
    c: Equal(g55,g57)
    c: InternalAlignment(g55,g58)
    c: InternalAlignment(g56,g58)
    c: InternalAlignment(g57,g58)
    c: InternalAlignment(g59,g58)
    c: InternalAlignment(g60,g58)
    c: Block(g58)
    c: Weight(g61) = 1
    c: Equal(g61,g62)
    c: Equal(g61,g63)
    c: InternalAlignment(g61,g64)
    c: InternalAlignment(g62,g64)
    c: InternalAlignment(g63,g64)
    c: InternalAlignment(g65,g64)
    c: InternalAlignment(g66,g64)
    c: Block(g64)
    c: Weight(g67) = 1
    c: Equal(g67,g68)
    c: Equal(g67,g69)
    c: InternalAlignment(g67,g70)
    c: InternalAlignment(g68,g70)
    c: InternalAlignment(g69,g70)
    c: InternalAlignment(g71,g70)
    c: InternalAlignment(g72,g70)
    c: Block(g70)
    c: Weight(g73) = 1
    c: Equal(g73,g74)
    c: Equal(g73,g75)
    c: InternalAlignment(g73,g76)
    c: InternalAlignment(g74,g76)
    c: InternalAlignment(g75,g76)
    c: InternalAlignment(g77,g76)
    c: InternalAlignment(g78,g76)
    c: Weight(g79) = 1
    c: Equal(g79,g80)
    c: Equal(g79,g81)
    c: InternalAlignment(g79,g82)
    c: InternalAlignment(g80,g82)
    c: InternalAlignment(g81,g82)
    c: InternalAlignment(g83,g82)
    c: InternalAlignment(g84,g82)
    c: Block(g76)
    c: Block(g82)
    c: Coincident(g85,g76)
    c: Coincident(g85,g82)
    c: Vertical(g85)
    c: Coincident(g86,g76)
    c: Coincident(g86,g58)
    c: Coincident(g87,g58)
    c: Coincident(g87,g82)
    c: Weight(g88) = 1
    c: Equal(g88,g89)
    c: Equal(g88,g90)
    c: InternalAlignment(g88,g91)
    c: InternalAlignment(g89,g91)
    c: InternalAlignment(g90,g91)
    c: InternalAlignment(g92,g91)
    c: InternalAlignment(g93,g91)
    c: Weight(g94) = 1
    c: Equal(g94,g95)
    c: Equal(g94,g96)
    c: InternalAlignment(g94,g97)
    c: InternalAlignment(g95,g97)
    c: InternalAlignment(g96,g97)
    c: InternalAlignment(g98,g97)
    c: InternalAlignment(g99,g97)
    c: Block(g91)
    c: Block(g97)
    c: Coincident(g100,g91)
    c: Coincident(g100,g97)
    c: Vertical(g100)
    c: Coincident(g101,g91)
    c: Coincident(g101,g52)
    c: Coincident(g102,g52)
    c: Coincident(g102,g97)
    c: Weight(g103) = 1
    c: Equal(g103,g104)
    c: Equal(g103,g105)
    c: InternalAlignment(g103,g106)
    c: InternalAlignment(g104,g106)
    c: InternalAlignment(g105,g106)
    c: InternalAlignment(g107,g106)
    c: InternalAlignment(g108,g106)
    c: Weight(g109) = 1
    c: Equal(g109,g110)
    c: Equal(g109,g111)
    c: InternalAlignment(g109,g112)
    c: InternalAlignment(g110,g112)
    c: InternalAlignment(g111,g112)
    c: InternalAlignment(g113,g112)
    c: InternalAlignment(g114,g112)
    c: Block(g106)
    c: Block(g112)
    c: Coincident(g115,g106)
    c: Coincident(g115,g112)
    c: Vertical(g115)
    c: Coincident(g116,g112)
    c: Coincident(g116,g70)
    c: Coincident(g117,g70)
    c: Coincident(g117,g106)
    c: Weight(g118) = 1
    c: Equal(g118,g119)
    c: Equal(g118,g120)
    c: InternalAlignment(g118,g121)
    c: InternalAlignment(g119,g121)
    c: InternalAlignment(g120,g121)
    c: InternalAlignment(g122,g121)
    c: InternalAlignment(g123,g121)
    c: Weight(g124) = 1
    c: Equal(g124,g125)
    c: Equal(g124,g126)
    c: InternalAlignment(g124,g127)
    c: InternalAlignment(g125,g127)
    c: InternalAlignment(g126,g127)
    c: InternalAlignment(g128,g127)
    c: InternalAlignment(g129,g127)
    c: Block(g121)
    c: Block(g127)
    c: Coincident(g130,g121)
    c: Coincident(g130,g127)
    c: Vertical(g130)
    c: Coincident(g131,g127)
    c: Coincident(g131,g64)
    c: Coincident(g132,g64)
    c: Coincident(g132,g121)
    c: Weight(g133) = 1
    c: Equal(g133,g134)
    c: Equal(g133,g135)
    c: InternalAlignment(g133,g136)
    c: InternalAlignment(g134,g136)
    c: InternalAlignment(g135,g136)
    c: InternalAlignment(g137,g136)
    c: InternalAlignment(g138,g136)
    c: Weight(g139) = 1
    c: Equal(g139,g140)
    c: Equal(g139,g141)
    c: InternalAlignment(g139,g142)
    c: InternalAlignment(g140,g142)
    c: InternalAlignment(g141,g142)
    c: InternalAlignment(g143,g142)
    c: InternalAlignment(g144,g142)
    c: Weight(g145) = 1
    c: Equal(g145,g146)
    c: Equal(g145,g147)
    c: InternalAlignment(g145,g148)
    c: InternalAlignment(g146,g148)
    c: InternalAlignment(g147,g148)
    c: InternalAlignment(g149,g148)
    c: InternalAlignment(g150,g148)
    c: Weight(g151) = 1
    c: Equal(g151,g152)
    c: Equal(g151,g153)
    c: InternalAlignment(g151,g154)
    c: InternalAlignment(g152,g154)
    c: InternalAlignment(g153,g154)
    c: InternalAlignment(g155,g154)
    c: InternalAlignment(g156,g154)
    c: Block(g154)
    c: Block(g148)
    c: Block(g142)
    c: Block(g136)
    c: Coincident(g157,g31)
    c: Coincident(g157,g154)
    c: Coincident(g158,g154)
    c: Coincident(g158,g148)
    c: Horizontal(g158)
    c: Coincident(g159,g148)
    c: Coincident(g159,g31)
    c: Vertical(g159)
    c: Coincident(g160,g25)
    c: Coincident(g160,g142)
    c: Vertical(g160)
    c: Coincident(g161,g142)
    c: Coincident(g161,g136)
    c: Horizontal(g161)
    c: Coincident(g162,g136)
    c: Coincident(g162,g25)
    c: Weight(g163) = 1
    c: Equal(g163,g164)
    c: Equal(g163,g165)
    c: InternalAlignment(g163,g166)
    c: InternalAlignment(g164,g166)
    c: InternalAlignment(g165,g166)
    c: InternalAlignment(g167,g166)
    c: InternalAlignment(g168,g166)
    c: Weight(g169) = 1
    c: Equal(g169,g170)
    c: Equal(g169,g171)
    c: InternalAlignment(g169,g172)
    c: InternalAlignment(g170,g172)
    c: InternalAlignment(g171,g172)
    c: InternalAlignment(g173,g172)
    c: InternalAlignment(g174,g172)
    c: Weight(g175) = 1
    c: Equal(g175,g176)
    c: Equal(g175,g177)
    c: InternalAlignment(g175,g178)
    c: InternalAlignment(g176,g178)
    c: InternalAlignment(g177,g178)
    c: InternalAlignment(g179,g178)
    c: InternalAlignment(g180,g178)
    c: Weight(g181) = 1
    c: Equal(g181,g182)
    c: Equal(g181,g183)
    c: InternalAlignment(g181,g184)
    c: InternalAlignment(g182,g184)
    c: InternalAlignment(g183,g184)
    c: InternalAlignment(g185,g184)
    c: InternalAlignment(g186,g184)
    c: Block(g184)
    c: Block(g178)
    c: Block(g172)
    c: Block(g166)
    c: Coincident(g187,g184)
    c: Coincident(g187,g178)
    c: Horizontal(g187)
    c: Coincident(g188,g178)
    c: Coincident(g188,g13)
    c: Vertical(g188)
    c: Coincident(g189,g19)
    c: Coincident(g189,g172)
    c: Vertical(g189)
    c: Coincident(g190,g172)
    c: Coincident(g190,g166)
    c: Horizontal(g190)
    c: Coincident(g191,g166)
    c: Coincident(g191,g19)
    c: Coincident(g192,g13)
    c: Weight(g193) = 1
    c: Equal(g193,g194)
    c: Equal(g193,g195)
    c: InternalAlignment(g193,g196)
    c: InternalAlignment(g194,g196)
    c: InternalAlignment(g195,g196)
    c: InternalAlignment(g197,g196)
    c: InternalAlignment(g198,g196)
    c: Weight(g199) = 1
    c: Equal(g199,g200)
    c: Equal(g199,g201)
    c: InternalAlignment(g199,g202)
    c: InternalAlignment(g200,g202)
    c: InternalAlignment(g201,g202)
    c: InternalAlignment(g203,g202)
    c: InternalAlignment(g204,g202)
    c: Block(g202)
    c: Block(g196)
    c: Coincident(g205,g202)
    c: Coincident(g205,g37)
    c: Coincident(g206,g37)
    c: Coincident(g206,g196)
    c: Coincident(g207,g196)
    c: Coincident(g207,g202)
    c: Vertical(g207)
    c: Weight(g208) = 1
    c: Equal(g208,g209)
    c: Equal(g208,g210)
    c: InternalAlignment(g208,g211)
    c: InternalAlignment(g209,g211)
    c: InternalAlignment(g210,g211)
    c: InternalAlignment(g212,g211)
    c: InternalAlignment(g213,g211)
    c: Weight(g214) = 1
    c: Equal(g214,g215)
    c: Equal(g214,g216)
    c: InternalAlignment(g214,g217)
    c: InternalAlignment(g215,g217)
    c: InternalAlignment(g216,g217)
    c: InternalAlignment(g218,g217)
    c: InternalAlignment(g219,g217)
    c: Block(g217)
    c: Block(g211)
    c: Coincident(g220,g211)
    c: Coincident(g220,g43)
    c: Coincident(g221,g43)
    c: Coincident(g221,g217)
    c: Coincident(g222,g217)
    c: Coincident(g222,g211)
    c: Vertical(g222)
    c: Horizontal(g223)
    c: Block(g223)
    c: Vertical(g224)
    c: Block(g224)
    c: Block(g225)
    c: Weight(g226) = 1
    c: Equal(g226,g227)
    c: Equal(g226,g228)
    c: InternalAlignment(g226,g229)
    c: InternalAlignment(g227,g229)
    c: InternalAlignment(g228,g229)
    c: InternalAlignment(g230,g229)
    c: InternalAlignment(g231,g229)
    c: Weight(g232) = 1
    c: Equal(g232,g233)
    c: Equal(g232,g234)
    c: InternalAlignment(g232,g235)
    c: InternalAlignment(g233,g235)
    c: InternalAlignment(g234,g235)
    c: InternalAlignment(g236,g235)
    c: InternalAlignment(g237,g235)
    c: Weight(g238) = 1
    c: Equal(g238,g239)
    c: Equal(g238,g240)
    c: InternalAlignment(g238,g241)
    c: InternalAlignment(g239,g241)
    c: InternalAlignment(g240,g241)
    c: InternalAlignment(g242,g241)
    c: InternalAlignment(g243,g241)
    c: Weight(g244) = 1
    c: Equal(g244,g245)
    c: Equal(g244,g246)
    c: InternalAlignment(g244,g247)
    c: InternalAlignment(g245,g247)
    c: InternalAlignment(g246,g247)
    c: InternalAlignment(g248,g247)
    c: InternalAlignment(g249,g247)
    c: Block(g229)
    c: Block(g235)
    c: Block(g241)
    c: Block(g247)
    c: Coincident(g250,g235)
    c: Coincident(g250,g229)
    c: Horizontal(g250)
    c: Block(g192)
    c: Weight(g251) = 1
    c: Equal(g251,g252)
    c: Equal(g251,g253)
    c: InternalAlignment(g251,g254)
    c: InternalAlignment(g252,g254)
    c: InternalAlignment(g253,g254)
    c: InternalAlignment(g255,g254)
    c: InternalAlignment(g256,g254)
    c: Weight(g257) = 1
    c: Equal(g257,g258)
    c: Equal(g257,g259)
    c: InternalAlignment(g257,g260)
    c: InternalAlignment(g258,g260)
    c: InternalAlignment(g259,g260)
    c: InternalAlignment(g261,g260)
    c: InternalAlignment(g262,g260)
    c: Block(g254)
    c: Block(g260)
    c: Coincident(g263,g254)
    c: Coincident(g263,g260)
    c: Weight(g264) = 1
    c: Equal(g264,g265)
    c: Equal(g264,g266)
    c: InternalAlignment(g264,g267)
    c: InternalAlignment(g265,g267)
    c: InternalAlignment(g266,g267)
    c: InternalAlignment(g268,g267)
    c: InternalAlignment(g269,g267)
    c: Weight(g270) = 1
    c: Equal(g270,g271)
    c: Equal(g270,g272)
    c: InternalAlignment(g270,g273)
    c: InternalAlignment(g271,g273)
    c: InternalAlignment(g272,g273)
    c: InternalAlignment(g274,g273)
    c: InternalAlignment(g275,g273)
    c: Weight(g276) = 1
    c: Equal(g276,g277)
    c: Equal(g276,g278)
    c: InternalAlignment(g276,g279)
    c: InternalAlignment(g277,g279)
    c: InternalAlignment(g278,g279)
    c: InternalAlignment(g280,g279)
    c: InternalAlignment(g281,g279)
    c: Block(g279)
    c: Block(g273)
    c: Block(g267)
    c: Coincident(g282,g273)
    c: Coincident(g282,g267)
    c: Coincident(g283,g267)
    c: Coincident(g283,g279)
    c: Vertical(g283)
    c: Coincident(g284,g279)
    c: Coincident(g284,g273)
    c: Horizontal(g284)
    c: Weight(g285) = 1
    c: Equal(g285,g286)
    c: InternalAlignment(g285,g287)
    c: InternalAlignment(g286,g287)
    c: InternalAlignment(g288,g287)
    c: InternalAlignment(g289,g287)
    c: Weight(g290) = 1
    c: InternalAlignment(g291,g293)
    c: InternalAlignment(g292,g293)
    c: InternalAlignment(g294,g293)
    c: InternalAlignment(g295,g293)
    c: Weight(g296) = 1
    c: Equal(g296,g297)
    c: Equal(g296,g298)
    c: InternalAlignment(g296,g299)
    c: InternalAlignment(g297,g299)
    c: InternalAlignment(g298,g299)
    c: InternalAlignment(g300,g299)
    c: InternalAlignment(g301,g299)
    c: Equal(g302,g303)
    c: Equal(g302,g304)
    c: InternalAlignment(g302,g305)
    c: InternalAlignment(g303,g305)
    c: InternalAlignment(g304,g305)
    c: InternalAlignment(g306,g305)
    c: InternalAlignment(g307,g305)
    c: Block(g293)
    c: Block(g299)
    c: Block(g305)
    c: Block(g287)
    c: Coincident(g308,g287)
    c: Coincident(g308,g293)
    c: Horizontal(g308)
    c: Coincident(g309,g293)
    c: Coincident(g309,g299)
    c: Vertical(g309)
    c: Coincident(g310,g299)
    c: Coincident(g310,g305)
    c: Horizontal(g310)
    c: Coincident(g311,g305)
    c: Coincident(g311,g287)
    c: Weight(g312) = 1
    c: Equal(g312,g313)
    c: Equal(g312,g314)
    c: InternalAlignment(g312,g315)
    c: InternalAlignment(g313,g315)
    c: InternalAlignment(g314,g315)
    c: InternalAlignment(g316,g315)
    c: InternalAlignment(g317,g315)
    c: Weight(g318) = 1
    c: Equal(g318,g319)
    c: Equal(g318,g320)
    c: InternalAlignment(g318,g321)
    c: InternalAlignment(g319,g321)
    c: InternalAlignment(g320,g321)
    c: InternalAlignment(g322,g321)
    c: InternalAlignment(g323,g321)
    c: Weight(g324) = 1
    c: Equal(g324,g325)
    c: Equal(g324,g326)
    c: InternalAlignment(g324,g327)
    c: InternalAlignment(g325,g327)
    c: InternalAlignment(g326,g327)
    c: InternalAlignment(g328,g327)
    c: InternalAlignment(g329,g327)
    c: Block(g327)
    c: Block(g321)
    c: Block(g315)
    c: Coincident(g330,g327)
    c: Coincident(g330,g321)
    c: Horizontal(g330)
    c: Coincident(g331,g321)
    c: Coincident(g331,g315)
    c: Vertical(g331)
    c: Coincident(g332,g315)
    c: Coincident(g332,g327)
    c: InternalAlignment(g333,g334)
    c: InternalAlignment(g335,g334)
    c: InternalAlignment(g336,g334)
    c: Block(g334)
    c: Equal(g337,g338)
    c: Equal(g337,g339)
    c: InternalAlignment(g337,g340)
    c: InternalAlignment(g338,g340)
    c: InternalAlignment(g339,g340)
    c: InternalAlignment(g341,g340)
    c: InternalAlignment(g342,g340)
    c: Block(g340)
    c: Coincident(g343,g334)
    c: Horizontal(g343)
    c: Block(g343)
    c: Coincident(g344,g334)
    c: Coincident(g344,g260)
    c: Vertical(g344)
    c: Coincident(g345,g340)
    c: Coincident(g345,g254)
    c: Vertical(g345)
    c: Coincident(g347,g5)
    c: Coincident(g348,g5)
    c: Block(g346)
    c: Block(g5)
    c: Block(g348)
    c: Block(g347)
    c: Distance(g344) = 119.89
FEATURE [Sketcher::SketchObject] Sketch001
  FullyConstrained = true
  MapMode = 4
  Placement = pos=(0,0,0) rot=(0.57735,0.57735,0.57735;2.0944rad)
  Support = -> [Sketch]
  sketch-geometry (46):
    g0: BSplineCurve PolesCount=3 KnotsCount=2 Degree=2 IsPeriodic=0
    g1: ArcOfCircle CenterX=73.1223 CenterY=-32.291 CenterZ=0 NormalX=0 NormalY=0 NormalZ=1 AngleXU=0 Radius=13 StartAngle=5.92268 EndAngle=9.06428
    g2: ArcOfCircle CenterX=66.7816 CenterY=-49.1439 CenterZ=0 NormalX=0 NormalY=0 NormalZ=1 AngleXU=0 Radius=13 StartAngle=2.78068 EndAngle=5.92131
    g3: ArcOfCircle CenterX=55.9263 CenterY=-78.1807 CenterZ=0 NormalX=0 NormalY=0 NormalZ=1 AngleXU=0 Radius=13 StartAngle=5.92268 EndAngle=9.06428
    g4: ArcOfCircle CenterX=49.5884 CenterY=-95.0342 CenterZ=0 NormalX=0 NormalY=0 NormalZ=1 AngleXU=0 Radius=13 StartAngle=2.78068 EndAngle=5.92131
    g5: ArcOfCircle CenterX=38.7206 CenterY=-124.067 CenterZ=0 NormalX=0 NormalY=0 NormalZ=1 AngleXU=0 Radius=13 StartAngle=5.92268 EndAngle=9.06428
    g6: ArcOfCircle CenterX=32.3875 CenterY=-140.92 CenterZ=0 NormalX=0 NormalY=0 NormalZ=1 AngleXU=0 Radius=13 StartAngle=2.78068 EndAngle=5.92131
    g7: ArcOfCircle CenterX=21.4715 CenterY=-169.934 CenterZ=0 NormalX=0 NormalY=0 NormalZ=1 AngleXU=0 Radius=13 StartAngle=5.92268 EndAngle=9.06428
    g8: ArcOfCircle CenterX=15.1336 CenterY=-186.787 CenterZ=0 NormalX=0 NormalY=0 NormalZ=1 AngleXU=0 Radius=13 StartAngle=2.78068 EndAngle=5.92131
    g9-g12: Circle x4 (B-spline internal-alignment scaffolding for g13; pole/knot coordinates omitted)
    g13: BSplineCurve PolesCount=4 KnotsCount=2 Degree=3 IsPeriodic=0
    g14: GeomPoint X=28.8094 Y=-19.0875 Z=0
    g15: GeomPoint X=47.0443 Y=-50.4712 Z=0
    g16: Circle CenterX=53.5586 CenterY=-23.2695 CenterZ=0 NormalX=0 NormalY=0 NormalZ=1 AngleXU=0 Radius=3.24518
    g17: Circle CenterX=-195.441 CenterY=-127.082 CenterZ=0 NormalX=0 NormalY=0 NormalZ=1 AngleXU=0 Radius=1
    g18: Circle CenterX=-8.24091 CenterY=-197.481 CenterZ=0 NormalX=0 NormalY=0 NormalZ=1 AngleXU=0 Radius=1
    g19: Circle CenterX=12.8789 CenterY=-141.321 CenterZ=0 NormalX=0 NormalY=0 NormalZ=1 AngleXU=0 Radius=1
    g20: BSplineCurve PolesCount=3 KnotsCount=2 Degree=2 IsPeriodic=0
    g21: GeomPoint X=-195.441 Y=-127.082 Z=0
    g22: GeomPoint X=12.8789 Y=-141.321 Z=0
    g23: Circle CenterX=-12.8016 CenterY=-179.036 CenterZ=0 NormalX=0 NormalY=0 NormalZ=1 AngleXU=0 Radius=10.5072
    g24: Circle CenterX=0.933922 CenterY=-166.43 CenterZ=0 NormalX=0 NormalY=0 NormalZ=1 AngleXU=0 Radius=3.26661
    g25: Circle CenterX=-33.5518 CenterY=-176.44 CenterZ=0 NormalX=0 NormalY=0 NormalZ=1 AngleXU=0 Radius=5.64388
    g26: Circle CenterX=-47.2366 CenterY=-173.859 CenterZ=0 NormalX=0 NormalY=0 NormalZ=1 AngleXU=0 Radius=3.01653
    g27: Circle CenterX=-56.2595 CenterY=-171.456 CenterZ=0 NormalX=0 NormalY=0 NormalZ=1 AngleXU=0 Radius=2.12826
    g28: ArcOfCircle CenterX=51.2151 CenterY=-198.473 CenterZ=0 NormalX=0 NormalY=0 NormalZ=1 AngleXU=0 Radius=20 StartAngle=2.78189 EndAngle=4.35269
    g29: LineSegment StartX=32.4951 StartY=-191.433 StartZ=0 EndX=94.6578 EndY=-26.1352 EndZ=0
    g30: LineSegment StartX=43.1192 StartY=-220.001 StartZ=0 EndX=-196.497 EndY=-129.89 EndZ=0
    g31: LineSegment StartX=43.1192 StartY=-220.001 StartZ=0 EndX=44.1752 EndY=-217.193 EndZ=0
    g32: LineSegment StartX=117.223 StartY=-19.0875 StartZ=0 EndX=117.223 EndY=-16.0875 EndZ=0
    g33: LineSegment StartX=117.223 StartY=-16.0875 StartZ=0 EndX=17.2232 EndY=-16.0875 EndZ=0
    g34: LineSegment StartX=17.2232 StartY=-16.0875 StartZ=0 EndX=17.2232 EndY=-19.0875 EndZ=0
    g35: LineSegment StartX=28.8094 StartY=-19.0875 StartZ=0 EndX=17.2232 EndY=-19.0875 EndZ=0
    g36: LineSegment StartX=47.0443 StartY=-50.4712 StartZ=0 EndX=12.8789 EndY=-141.321 EndZ=0
    g37: LineSegment StartX=-195.441 StartY=-127.082 StartZ=0 EndX=-196.497 EndY=-129.89 EndZ=0
    g38: LineSegment StartX=85.2866 StartY=-36.8766 StartZ=0 EndX=78.9396 EndY=-53.7463 EndZ=0
    g39: LineSegment StartX=60.9579 StartY=-27.7053 StartZ=0 EndX=54.6191 EndY=-44.5532 EndZ=0
    g40: LineSegment StartX=68.0907 StartY=-82.7664 StartZ=0 EndX=61.7465 EndY=-99.6365 EndZ=0
    g41: LineSegment StartX=43.7619 StartY=-73.595 StartZ=0 EndX=37.426 EndY=-90.4435 EndZ=0
    g42: LineSegment StartX=50.885 StartY=-128.652 StartZ=0 EndX=44.5456 EndY=-145.522 EndZ=0
    g43: LineSegment StartX=26.5562 StartY=-119.481 StartZ=0 EndX=20.2251 EndY=-136.329 EndZ=0
    g44: LineSegment StartX=9.3071 StartY=-165.349 StartZ=0 EndX=2.97115 EndY=-182.197 EndZ=0
    g45: LineSegment StartX=33.6358 StartY=-174.52 StartZ=0 EndX=27.2917 EndY=-191.39 EndZ=0
  constraints (71):
    c: Block(g0)
    c: Block(g1)
    c: Block(g2)
    c: Block(g4)
    c: Block(g3)
    c: Block(g6)
    c: Block(g5)
    c: Block(g8)
    c: Block(g7)
    c: Weight(g9) = 1
    c: Equal(g9,g10)
    c: Equal(g9,g11)
    c: Equal(g9,g12)
    c: InternalAlignment(g9-g12 -> g13) x4
    c: InternalAlignment(g14,g13)
    c: InternalAlignment(g15,g13)
    c: Block(g16)
    c: Weight(g17) = 1
    c: Equal(g17,g18)
    c: Equal(g17,g19)
    c: InternalAlignment(g17,g20)
    c: InternalAlignment(g18,g20)
    c: InternalAlignment(g19,g20)
    c: InternalAlignment(g21,g20)
    c: InternalAlignment(g22,g20)
    c: Block(g20)
    c: Block(g23)
    c: Block(g24)
    c: Block(g25)
    c: Block(g26)
    c: Block(g27)
    c: Block(g28)
    c: Coincident(g29,g28)
    c: Coincident(g29,g0)
    c: Block(g13)
    c: Coincident(g31,g30)
    c: Coincident(g31,g28)
    c: Block(g31)
    c: Coincident(g32,g0)
    c: Vertical(g32)
    c: Coincident(g33,g32)
    c: Horizontal(g33)
    c: Coincident(g34,g33)
    c: Vertical(g34)
    c: Block(g33)
    c: Coincident(g35,g13)
    c: Coincident(g35,g34)
    c: Horizontal(g35)
    c: Coincident(g36,g13)
    c: Coincident(g36,g20)
    c: Coincident(g37,g20)
    c: Coincident(g37,g30)
    c: Block(g30)
    c: Coincident(g38,g1)
    c: Coincident(g38,g2)
    c: Coincident(g39,g1)
    c: Coincident(g39,g2)
    c: Coincident(g40,g3)
    c: Coincident(g40,g4)
    c: Coincident(g41,g3)
    c: Coincident(g41,g4)
    c: Coincident(g42,g5)
    c: Coincident(g42,g6)
    c: Coincident(g43,g5)
    c: Coincident(g43,g6)
    c: Coincident(g44,g7)
    c: Coincident(g44,g8)
    c: Coincident(g45,g7)
    c: Coincident(g45,g8)
    c: Distance(g30) = 256
    c: Distance(g33) = 100
FEATURE [Part::Extrusion] Extrude002
  Base = -> Sketch001
  Dir = (1,0,0)
  DirMode = 2
  FaceMakerClass = Part::FaceMakerBullseye
  LengthFwd = 8
  LengthRev = 0
  Solid = true
  Symmetric = false
FEATURE [Sketcher::SketchObject] Sketch002
  FullyConstrained = true
  sketch-geometry (20):
    g0: LineSegment StartX=-2.77179 StartY=-200.304 StartZ=0 EndX=5.22821 EndY=-200.304 EndZ=0
    g1: LineSegment StartX=5.22821 StartY=-200.304 StartZ=0 EndX=5.22821 EndY=-197.304 EndZ=0
    g2: LineSegment StartX=-2.77179 StartY=-200.304 StartZ=0 EndX=-2.77179 EndY=-197.304 EndZ=0
    g3: LineSegment StartX=5.22821 StartY=-197.304 StartZ=0 EndX=8.22821 EndY=-197.304 EndZ=0
    g4: LineSegment StartX=-2.77179 StartY=-197.304 StartZ=0 EndX=-5.77179 EndY=-197.304 EndZ=0
    g5: LineSegment StartX=19.2282 StartY=-203.304 StartZ=0 EndX=19.2282 EndY=-206.304 EndZ=0
    g6: LineSegment StartX=-16.7718 StartY=-203.304 StartZ=0 EndX=-16.7718 EndY=-206.304 EndZ=0
    g7: LineSegment StartX=-16.7718 StartY=-206.304 StartZ=0 EndX=19.2282 EndY=-206.304 EndZ=0
    g8: Circle CenterX=-16.7718 CenterY=-203.304 CenterZ=0 NormalX=0 NormalY=0 NormalZ=1 AngleXU=0 Radius=1
    g9: Circle CenterX=-5.77179 CenterY=-203.304 CenterZ=0 NormalX=0 NormalY=0 NormalZ=1 AngleXU=0 Radius=1
    g10: Circle CenterX=-5.77179 CenterY=-197.304 CenterZ=0 NormalX=0 NormalY=0 NormalZ=1 AngleXU=0 Radius=1
    g11: BSplineCurve PolesCount=3 KnotsCount=2 Degree=2 IsPeriodic=0
    g12: GeomPoint X=-16.7718 Y=-203.304 Z=0
    g13: GeomPoint X=-5.77179 Y=-197.304 Z=0
    g14: Circle CenterX=19.2282 CenterY=-203.304 CenterZ=0 NormalX=0 NormalY=0 NormalZ=1 AngleXU=0 Radius=1
    g15: Circle CenterX=8.22821 CenterY=-203.304 CenterZ=0 NormalX=0 NormalY=0 NormalZ=1 AngleXU=0 Radius=1
    g16: Circle CenterX=8.22821 CenterY=-197.304 CenterZ=0 NormalX=0 NormalY=0 NormalZ=1 AngleXU=0 Radius=1
    g17: BSplineCurve PolesCount=3 KnotsCount=2 Degree=2 IsPeriodic=0
    g18: GeomPoint X=19.2282 Y=-203.304 Z=0
    g19: GeomPoint X=8.22821 Y=-197.304 Z=0
  constraints (41):
    c: Horizontal(g0)
    c: Distance(g0) = 8
    c: Coincident(g1,g0)
    c: Vertical(g1)
    c: Distance(g1) = 3
    c: Coincident(g2,g0)
    c: Vertical(g2)
    c: Distance(g2) = 3
    c: Coincident(g3,g1)
    c: Horizontal(g3)
    c: Distance(g3) = 3
    c: Coincident(g4,g2)
    c: Horizontal(g4)
    c: Distance(g4) = 3
    c: Vertical(g5)
    c: Vertical(g6)
    c: Coincident(g7,g6)
    c: Coincident(g7,g5)
    c: Weight(g8) = 1
    c: Equal(g8,g9)
    c: Equal(g8,g10)
    c: Coincident(g11,g4)
    c: InternalAlignment(g8,g11)
    c: InternalAlignment(g9,g11)
    c: InternalAlignment(g10,g11)
    c: InternalAlignment(g12,g11)
    c: InternalAlignment(g13,g11)
    c: Coincident(g17,g5)
    c: Weight(g14) = 1
    c: Equal(g14,g15)
    c: Equal(g14,g16)
    c: Coincident(g17,g3)
    c: InternalAlignment(g14,g17)
    c: InternalAlignment(g15,g17)
    c: InternalAlignment(g16,g17)
    c: InternalAlignment(g18,g17)
    c: InternalAlignment(g19,g17)
    c: Block(g7)
    c: Block(g17)
    c: Block(g11)
    c: Block(g6)
FEATURE [Part::Extrusion] Extrude003
  Base = -> Sketch002
  Dir = (0,0,1)
  DirMode = 2
  FaceMakerClass = Part::FaceMakerBullseye
  LengthFwd = 260
  LengthRev = 0
  Solid = true
  Symmetric = false
FEATURE [Sketcher::SketchObject] Sketch003
  FullyConstrained = false
  sketch-geometry (423):
    g0: LineSegment StartX=-42.9272 StartY=136.221 StartZ=0 EndX=-42.9272 EndY=-103.779 EndZ=0
    g1: LineSegment StartX=407.073 StartY=136.221 StartZ=0 EndX=407.073 EndY=-103.779 EndZ=0
    g2: ArcOfCircle CenterX=-26.9272 CenterY=-83.7794 CenterZ=0 NormalX=0 NormalY=0 NormalZ=1 AngleXU=0 Radius=8 StartAngle=3.14159 EndAngle=6.28319
    g3: ArcOfCircle CenterX=391.073 CenterY=-83.7794 CenterZ=0 NormalX=0 NormalY=0 NormalZ=1 AngleXU=0 Radius=8 StartAngle=3.14159 EndAngle=6.28319
    g4: Circle CenterX=175.022 CenterY=27.0628 CenterZ=0 NormalX=0 NormalY=0 NormalZ=1 AngleXU=0 Radius=1
    g5: Circle CenterX=179.022 CenterY=24.8665 CenterZ=0 NormalX=0 NormalY=0 NormalZ=1 AngleXU=0 Radius=1
    g6: Circle CenterX=179.022 CenterY=27.0628 CenterZ=0 NormalX=0 NormalY=0 NormalZ=1 AngleXU=0 Radius=1
    g7: BSplineCurve PolesCount=3 KnotsCount=2 Degree=2 IsPeriodic=0
    g8: GeomPoint X=175.022 Y=27.0628 Z=0
    g9: GeomPoint X=179.022 Y=27.0628 Z=0
    g10: Circle CenterX=189.124 CenterY=27.0628 CenterZ=0 NormalX=0 NormalY=0 NormalZ=1 AngleXU=0 Radius=1
    g11: Circle CenterX=185.124 CenterY=24.8665 CenterZ=0 NormalX=0 NormalY=0 NormalZ=1 AngleXU=0 Radius=1
    g12: Circle CenterX=185.124 CenterY=27.0628 CenterZ=0 NormalX=0 NormalY=0 NormalZ=1 AngleXU=0 Radius=1
    g13: BSplineCurve PolesCount=3 KnotsCount=2 Degree=2 IsPeriodic=0
    g14: GeomPoint X=189.124 Y=27.0628 Z=0
    g15: GeomPoint X=185.124 Y=27.0628 Z=0
    g16: Circle CenterX=175.022 CenterY=5.37834 CenterZ=0 NormalX=0 NormalY=0 NormalZ=1 AngleXU=0 Radius=1
    g17: Circle CenterX=179.022 CenterY=7.57463 CenterZ=0 NormalX=0 NormalY=0 NormalZ=1 AngleXU=0 Radius=1
    g18: Circle CenterX=179.022 CenterY=5.34704 CenterZ=0 NormalX=0 NormalY=0 NormalZ=1 AngleXU=0 Radius=1
    g19: BSplineCurve PolesCount=3 KnotsCount=2 Degree=2 IsPeriodic=0
    g20: GeomPoint X=175.022 Y=5.37834 Z=0
    g21: GeomPoint X=179.022 Y=5.34704 Z=0
    g22: Circle CenterX=189.124 CenterY=5.37834 CenterZ=0 NormalX=0 NormalY=0 NormalZ=1 AngleXU=0 Radius=1
    g23: Circle CenterX=185.124 CenterY=7.57463 CenterZ=0 NormalX=0 NormalY=0 NormalZ=1 AngleXU=0 Radius=1
    g24: Circle CenterX=185.124 CenterY=5.34704 CenterZ=0 NormalX=0 NormalY=0 NormalZ=1 AngleXU=0 Radius=1
    g25: BSplineCurve PolesCount=3 KnotsCount=2 Degree=2 IsPeriodic=0
    g26: GeomPoint X=189.124 Y=5.37834 Z=0
    g27: GeomPoint X=185.124 Y=5.34704 Z=0
    g28: Circle CenterX=165.871 CenterY=18.1458 CenterZ=0 NormalX=0 NormalY=0 NormalZ=1 AngleXU=0 Radius=1
    g29: Circle CenterX=169.377 CenterY=16.2206 CenterZ=0 NormalX=0 NormalY=0 NormalZ=1 AngleXU=0 Radius=1
    g30: Circle CenterX=165.871 CenterY=14.2954 CenterZ=0 NormalX=0 NormalY=0 NormalZ=1 AngleXU=0 Radius=1
    g31: BSplineCurve PolesCount=3 KnotsCount=2 Degree=2 IsPeriodic=0
    g32: GeomPoint X=165.871 Y=18.1458 Z=0
    g33: GeomPoint X=165.871 Y=14.2954 Z=0
    g34: Circle CenterX=198.275 CenterY=18.1458 CenterZ=0 NormalX=0 NormalY=0 NormalZ=1 AngleXU=0 Radius=1
    g35: Circle CenterX=194.768 CenterY=16.2206 CenterZ=0 NormalX=0 NormalY=0 NormalZ=1 AngleXU=0 Radius=1
    g36: Circle CenterX=198.275 CenterY=14.2954 CenterZ=0 NormalX=0 NormalY=0 NormalZ=1 AngleXU=0 Radius=1
    g37: BSplineCurve PolesCount=3 KnotsCount=2 Degree=2 IsPeriodic=0
    g38: GeomPoint X=198.275 Y=18.1458 Z=0
    g39: GeomPoint X=198.275 Y=14.2954 Z=0
    g40: LineSegment StartX=407.073 StartY=-103.779 StartZ=0 EndX=-42.9272 EndY=-103.779 EndZ=0
    g41: Circle CenterX=125.607 CenterY=54.1951 CenterZ=0 NormalX=0 NormalY=0 NormalZ=1 AngleXU=0 Radius=1
    g42: Circle CenterX=139.632 CenterY=46.4944 CenterZ=0 NormalX=0 NormalY=0 NormalZ=1 AngleXU=0 Radius=1
    g43: Circle CenterX=127.326 CenterY=56.7187 CenterZ=0 NormalX=0 NormalY=0 NormalZ=1 AngleXU=0 Radius=1
    g44: BSplineCurve PolesCount=3 KnotsCount=2 Degree=2 IsPeriodic=0
    g45: GeomPoint X=125.607 Y=54.1951 Z=0
    g46: GeomPoint X=127.326 Y=56.7187 Z=0
    g47: Circle CenterX=236.821 CenterY=56.7187 CenterZ=0 NormalX=0 NormalY=0 NormalZ=1 AngleXU=0 Radius=1
    g48: Circle CenterX=224.513 CenterY=46.4944 CenterZ=0 NormalX=0 NormalY=0 NormalZ=1 AngleXU=0 Radius=1
    g49: Circle CenterX=238.538 CenterY=54.1951 CenterZ=0 NormalX=0 NormalY=0 NormalZ=1 AngleXU=0 Radius=1
    g50: BSplineCurve PolesCount=3 KnotsCount=2 Degree=2 IsPeriodic=0
    g51: GeomPoint X=236.821 Y=56.7187 Z=0
    g52: GeomPoint X=238.538 Y=54.1951 Z=0
    g53: Circle CenterX=238.538 CenterY=-21.7539 CenterZ=0 NormalX=0 NormalY=0 NormalZ=1 AngleXU=0 Radius=1
    g54: Circle CenterX=224.513 CenterY=-14.0532 CenterZ=0 NormalX=0 NormalY=0 NormalZ=1 AngleXU=0 Radius=1
    g55: Circle CenterX=236.821 CenterY=-24.2775 CenterZ=0 NormalX=0 NormalY=0 NormalZ=1 AngleXU=0 Radius=1
    g56: BSplineCurve PolesCount=3 KnotsCount=2 Degree=2 IsPeriodic=0
    g57: GeomPoint X=238.538 Y=-21.7539 Z=0
    g58: GeomPoint X=236.821 Y=-24.2775 Z=0
    g59: Circle CenterX=125.607 CenterY=-21.7539 CenterZ=0 NormalX=0 NormalY=0 NormalZ=1 AngleXU=0 Radius=1
    g60: Circle CenterX=139.632 CenterY=-14.0532 CenterZ=0 NormalX=0 NormalY=0 NormalZ=1 AngleXU=0 Radius=1
    g61: Circle CenterX=127.325 CenterY=-24.2775 CenterZ=0 NormalX=0 NormalY=0 NormalZ=1 AngleXU=0 Radius=1
    g62: BSplineCurve PolesCount=3 KnotsCount=2 Degree=2 IsPeriodic=0
    g63: GeomPoint X=125.607 Y=-21.7539 Z=0
    g64: GeomPoint X=127.325 Y=-24.2775 Z=0
    g65: Circle CenterX=302.996 CenterY=111.695 CenterZ=0 NormalX=0 NormalY=0 NormalZ=1 AngleXU=0 Radius=1
    g66: Circle CenterX=306.073 CenterY=114.251 CenterZ=0 NormalX=0 NormalY=0 NormalZ=1 AngleXU=0 Radius=1
    g67: Circle CenterX=306.073 CenterY=110.251 CenterZ=0 NormalX=0 NormalY=0 NormalZ=1 AngleXU=0 Radius=1
    g68: BSplineCurve PolesCount=3 KnotsCount=2 Degree=2 IsPeriodic=0
    g69: GeomPoint X=302.996 Y=111.695 Z=0
    g70: GeomPoint X=306.073 Y=110.251 Z=0
    g71: Circle CenterX=306.073 CenterY=95.2763 CenterZ=0 NormalX=0 NormalY=0 NormalZ=1 AngleXU=0 Radius=1
    g72: Circle CenterX=306.073 CenterY=91.2763 CenterZ=0 NormalX=0 NormalY=0 NormalZ=1 AngleXU=0 Radius=1
    g73: Circle CenterX=302.567 CenterY=89.3511 CenterZ=0 NormalX=0 NormalY=0 NormalZ=1 AngleXU=0 Radius=1
    g74: BSplineCurve PolesCount=3 KnotsCount=2 Degree=2 IsPeriodic=0
    g75: GeomPoint X=306.073 Y=95.2763 Z=0
    g76: GeomPoint X=302.567 Y=89.3511 Z=0
    g77: LineSegment StartX=306.073 StartY=110.251 StartZ=0 EndX=306.073 EndY=95.2763 EndZ=0
    g78: LineSegment StartX=302.996 StartY=111.695 StartZ=0 EndX=236.821 EndY=56.7187 EndZ=0
    g79: LineSegment StartX=238.538 StartY=54.1951 StartZ=0 EndX=302.567 EndY=89.3511 EndZ=0
    g80: Circle CenterX=61.1496 CenterY=111.695 CenterZ=0 NormalX=0 NormalY=0 NormalZ=1 AngleXU=0 Radius=1
    g81: Circle CenterX=58.0728 CenterY=114.251 CenterZ=0 NormalX=0 NormalY=0 NormalZ=1 AngleXU=0 Radius=1
    g82: Circle CenterX=58.0728 CenterY=110.251 CenterZ=0 NormalX=0 NormalY=0 NormalZ=1 AngleXU=0 Radius=1
    g83: BSplineCurve PolesCount=3 KnotsCount=2 Degree=2 IsPeriodic=0
    g84: GeomPoint X=61.1496 Y=111.695 Z=0
    g85: GeomPoint X=58.0728 Y=110.251 Z=0
    g86: Circle CenterX=61.5791 CenterY=89.3511 CenterZ=0 NormalX=0 NormalY=0 NormalZ=1 AngleXU=0 Radius=1
    g87: Circle CenterX=58.0728 CenterY=91.2763 CenterZ=0 NormalX=0 NormalY=0 NormalZ=1 AngleXU=0 Radius=1
    g88: Circle CenterX=58.0728 CenterY=95.2763 CenterZ=0 NormalX=0 NormalY=0 NormalZ=1 AngleXU=0 Radius=1
    g89: BSplineCurve PolesCount=3 KnotsCount=2 Degree=2 IsPeriodic=0
    g90: GeomPoint X=61.5791 Y=89.3511 Z=0
    g91: GeomPoint X=58.0728 Y=95.2763 Z=0
    g92: LineSegment StartX=58.0728 StartY=110.251 StartZ=0 EndX=58.0728 EndY=95.2763 EndZ=0
    g93: LineSegment StartX=61.1496 StartY=111.695 StartZ=0 EndX=127.326 EndY=56.7187 EndZ=0
    g94: LineSegment StartX=125.607 StartY=54.1951 StartZ=0 EndX=61.5791 EndY=89.3511 EndZ=0
    g95: Circle CenterX=61.5791 CenterY=-56.9099 CenterZ=0 NormalX=0 NormalY=0 NormalZ=1 AngleXU=0 Radius=1
    g96: Circle CenterX=58.0728 CenterY=-58.8351 CenterZ=0 NormalX=0 NormalY=0 NormalZ=1 AngleXU=0 Radius=1
    g97: Circle CenterX=58.0728 CenterY=-62.8351 CenterZ=0 NormalX=0 NormalY=0 NormalZ=1 AngleXU=0 Radius=1
    g98: BSplineCurve PolesCount=3 KnotsCount=2 Degree=2 IsPeriodic=0
    g99: GeomPoint X=61.5791 Y=-56.9099 Z=0
    g100: GeomPoint X=58.0728 Y=-62.8351 Z=0
    g101: Circle CenterX=58.0728 CenterY=-77.8102 CenterZ=0 NormalX=0 NormalY=0 NormalZ=1 AngleXU=0 Radius=1
    g102: Circle CenterX=58.0728 CenterY=-81.8102 CenterZ=0 NormalX=0 NormalY=0 NormalZ=1 AngleXU=0 Radius=1
    g103: Circle CenterX=61.1496 CenterY=-79.2541 CenterZ=0 NormalX=0 NormalY=0 NormalZ=1 AngleXU=0 Radius=1
    g104: BSplineCurve PolesCount=3 KnotsCount=2 Degree=2 IsPeriodic=0
    g105: GeomPoint X=58.0728 Y=-77.8102 Z=0
    g106: GeomPoint X=61.1496 Y=-79.2541 Z=0
    g107: LineSegment StartX=58.0728 StartY=-62.8351 StartZ=0 EndX=58.0728 EndY=-77.8102 EndZ=0
    g108: LineSegment StartX=61.1496 StartY=-79.2541 StartZ=0 EndX=127.325 EndY=-24.2775 EndZ=0
    g109: LineSegment StartX=125.607 StartY=-21.7539 StartZ=0 EndX=61.5791 EndY=-56.9099 EndZ=0
    g110: Circle CenterX=302.567 CenterY=-56.9099 CenterZ=0 NormalX=0 NormalY=0 NormalZ=1 AngleXU=0 Radius=1
    g111: Circle CenterX=306.073 CenterY=-58.8351 CenterZ=0 NormalX=0 NormalY=0 NormalZ=1 AngleXU=0 Radius=1
    g112: Circle CenterX=306.073 CenterY=-62.8351 CenterZ=0 NormalX=0 NormalY=0 NormalZ=1 AngleXU=0 Radius=1
    g113: BSplineCurve PolesCount=3 KnotsCount=2 Degree=2 IsPeriodic=0
    g114: GeomPoint X=302.567 Y=-56.9099 Z=0
    g115: GeomPoint X=306.073 Y=-62.8351 Z=0
    g116: Circle CenterX=302.996 CenterY=-79.2541 CenterZ=0 NormalX=0 NormalY=0 NormalZ=1 AngleXU=0 Radius=1
    g117: Circle CenterX=306.073 CenterY=-81.8102 CenterZ=0 NormalX=0 NormalY=0 NormalZ=1 AngleXU=0 Radius=1
    g118: Circle CenterX=306.073 CenterY=-77.8102 CenterZ=0 NormalX=0 NormalY=0 NormalZ=1 AngleXU=0 Radius=1
    g119: BSplineCurve PolesCount=3 KnotsCount=2 Degree=2 IsPeriodic=0
    g120: GeomPoint X=302.996 Y=-79.2541 Z=0
    g121: GeomPoint X=306.073 Y=-77.8102 Z=0
    g122: LineSegment StartX=306.073 StartY=-62.8351 StartZ=0 EndX=306.073 EndY=-77.8102 EndZ=0
    g123: LineSegment StartX=302.996 StartY=-79.2541 StartZ=0 EndX=236.821 EndY=-24.2775 EndZ=0
    g124: LineSegment StartX=238.538 StartY=-21.7539 StartZ=0 EndX=302.567 EndY=-56.9099 EndZ=0
    g125: Circle CenterX=61.6457 CenterY=-88.8112 CenterZ=0 NormalX=0 NormalY=0 NormalZ=1 AngleXU=0 Radius=1
    g126: Circle CenterX=58.0728 CenterY=-91.7794 CenterZ=0 NormalX=0 NormalY=0 NormalZ=1 AngleXU=0 Radius=1
    g127: Circle CenterX=63.9135 CenterY=-91.7791 CenterZ=0 NormalX=0 NormalY=0 NormalZ=1 AngleXU=0 Radius=1
    g128: BSplineCurve PolesCount=3 KnotsCount=2 Degree=2 IsPeriodic=0
    g129: GeomPoint X=61.6457 Y=-88.8112 Z=0
    g130: GeomPoint X=63.9135 Y=-91.7791 Z=0
    g131: Circle CenterX=179.022 CenterY=-85.8163 CenterZ=0 NormalX=0 NormalY=0 NormalZ=1 AngleXU=0 Radius=1
    g132: Circle CenterX=179.022 CenterY=-91.7794 CenterZ=0 NormalX=0 NormalY=0 NormalZ=1 AngleXU=0 Radius=1
    g133: Circle CenterX=171.895 CenterY=-91.7791 CenterZ=0 NormalX=0 NormalY=0 NormalZ=1 AngleXU=0 Radius=1
    g134: BSplineCurve PolesCount=3 KnotsCount=2 Degree=2 IsPeriodic=0
    g135: GeomPoint X=179.022 Y=-85.8163 Z=0
    g136: GeomPoint X=171.895 Y=-91.7791 Z=0
    g137: Circle CenterX=185.124 CenterY=-86.2028 CenterZ=0 NormalX=0 NormalY=0 NormalZ=1 AngleXU=0 Radius=1
    g138: Circle CenterX=185.124 CenterY=-91.7794 CenterZ=0 NormalX=0 NormalY=0 NormalZ=1 AngleXU=0 Radius=1
    g139: Circle CenterX=191.747 CenterY=-91.7794 CenterZ=0 NormalX=0 NormalY=0 NormalZ=1 AngleXU=0 Radius=1
    g140: BSplineCurve PolesCount=3 KnotsCount=2 Degree=2 IsPeriodic=0
    g141: GeomPoint X=185.124 Y=-86.2028 Z=0
    g142: GeomPoint X=191.747 Y=-91.7794 Z=0
    g143: Circle CenterX=299.888 CenterY=-86.6413 CenterZ=0 NormalX=0 NormalY=0 NormalZ=1 AngleXU=0 Radius=1
    g144: Circle CenterX=306.073 CenterY=-91.7794 CenterZ=0 NormalX=0 NormalY=0 NormalZ=1 AngleXU=0 Radius=1
    g145: Circle CenterX=298.776 CenterY=-91.7794 CenterZ=0 NormalX=0 NormalY=0 NormalZ=1 AngleXU=0 Radius=1
    g146: BSplineCurve PolesCount=3 KnotsCount=2 Degree=2 IsPeriodic=0
    g147: GeomPoint X=299.888 Y=-86.6413 Z=0
    g148: GeomPoint X=298.776 Y=-91.7794 Z=0
    g149: LineSegment StartX=189.124 StartY=5.37834 StartZ=0 EndX=299.888 EndY=-86.6413 EndZ=0
    g150: LineSegment StartX=298.776 StartY=-91.7794 StartZ=0 EndX=191.747 EndY=-91.7794 EndZ=0
    g151: LineSegment StartX=185.124 StartY=-86.2028 StartZ=0 EndX=185.124 EndY=5.34704 EndZ=0
    g152: LineSegment StartX=179.022 StartY=5.34704 StartZ=0 EndX=179.022 EndY=-85.8163 EndZ=0
    g153: LineSegment StartX=171.895 StartY=-91.7791 StartZ=0 EndX=63.9135 EndY=-91.7791 EndZ=0
    g154: LineSegment StartX=61.6457 StartY=-88.8112 StartZ=0 EndX=175.022 EndY=5.37834 EndZ=0
    g155: Circle CenterX=302.073 CenterY=124.221 CenterZ=0 NormalX=0 NormalY=0 NormalZ=1 AngleXU=0 Radius=1
    g156: Circle CenterX=306.073 CenterY=124.221 CenterZ=0 NormalX=0 NormalY=0 NormalZ=1 AngleXU=0 Radius=1
    g157: Circle CenterX=302.996 CenterY=121.665 CenterZ=0 NormalX=0 NormalY=0 NormalZ=1 AngleXU=0 Radius=1
    g158: BSplineCurve PolesCount=3 KnotsCount=2 Degree=2 IsPeriodic=0
    g159: GeomPoint X=302.073 Y=124.221 Z=0
    g160: GeomPoint X=302.996 Y=121.665 Z=0
    g161: Circle CenterX=189.124 CenterY=124.221 CenterZ=0 NormalX=0 NormalY=0 NormalZ=1 AngleXU=0 Radius=1
    g162: Circle CenterX=185.124 CenterY=124.221 CenterZ=0 NormalX=0 NormalY=0 NormalZ=1 AngleXU=0 Radius=1
    g163: Circle CenterX=185.124 CenterY=120.221 CenterZ=0 NormalX=0 NormalY=0 NormalZ=1 AngleXU=0 Radius=1
    g164: BSplineCurve PolesCount=3 KnotsCount=2 Degree=2 IsPeriodic=0
    g165: GeomPoint X=189.124 Y=124.221 Z=0
    g166: GeomPoint X=185.124 Y=120.221 Z=0
    g167: Circle CenterX=175.022 CenterY=124.221 CenterZ=0 NormalX=0 NormalY=0 NormalZ=1 AngleXU=0 Radius=1
    g168: Circle CenterX=179.022 CenterY=124.221 CenterZ=0 NormalX=0 NormalY=0 NormalZ=1 AngleXU=0 Radius=1
    g169: Circle CenterX=179.022 CenterY=120.221 CenterZ=0 NormalX=0 NormalY=0 NormalZ=1 AngleXU=0 Radius=1
    g170: BSplineCurve PolesCount=3 KnotsCount=2 Degree=2 IsPeriodic=0
    g171: GeomPoint X=175.022 Y=124.221 Z=0
    g172: GeomPoint X=179.022 Y=120.221 Z=0
    g173: Circle CenterX=62.0728 CenterY=124.221 CenterZ=0 NormalX=0 NormalY=0 NormalZ=1 AngleXU=0 Radius=1
    g174: Circle CenterX=58.0728 CenterY=124.221 CenterZ=0 NormalX=0 NormalY=0 NormalZ=1 AngleXU=0 Radius=1
    g175: Circle CenterX=61.1496 CenterY=121.665 CenterZ=0 NormalX=0 NormalY=0 NormalZ=1 AngleXU=0 Radius=1
    g176: BSplineCurve PolesCount=3 KnotsCount=2 Degree=2 IsPeriodic=0
    g177: GeomPoint X=62.0728 Y=124.221 Z=0
    g178: GeomPoint X=61.1496 Y=121.665 Z=0
    g179: LineSegment StartX=179.022 StartY=120.221 StartZ=0 EndX=179.022 EndY=27.0628 EndZ=0
    g180: LineSegment StartX=185.124 StartY=27.0628 StartZ=0 EndX=185.124 EndY=120.221 EndZ=0
    g181: LineSegment StartX=302.996 StartY=121.665 StartZ=0 EndX=189.124 EndY=27.0628 EndZ=0
    g182: LineSegment StartX=175.022 StartY=27.0628 StartZ=0 EndX=61.1496 EndY=121.665 EndZ=0
    g183: Circle CenterX=61.5791 CenterY=75.4095 CenterZ=0 NormalX=0 NormalY=0 NormalZ=1 AngleXU=0 Radius=1
    g184: Circle CenterX=58.0728 CenterY=77.3346 CenterZ=0 NormalX=0 NormalY=0 NormalZ=1 AngleXU=0 Radius=1
    g185: Circle CenterX=58.0728 CenterY=73.3346 CenterZ=0 NormalX=0 NormalY=0 NormalZ=1 AngleXU=0 Radius=1
    g186: BSplineCurve PolesCount=3 KnotsCount=2 Degree=2 IsPeriodic=0
    g187: GeomPoint X=61.5791 Y=75.4095 Z=0
    g188: GeomPoint X=58.0728 Y=73.3346 Z=0
    g189: Circle CenterX=58.0728 CenterY=-40.8935 CenterZ=0 NormalX=0 NormalY=0 NormalZ=1 AngleXU=0 Radius=1
    g190: Circle CenterX=58.0728 CenterY=-44.8935 CenterZ=0 NormalX=0 NormalY=0 NormalZ=1 AngleXU=0 Radius=1
    g191: Circle CenterX=61.5791 CenterY=-42.9683 CenterZ=0 NormalX=0 NormalY=0 NormalZ=1 AngleXU=0 Radius=1
    g192: BSplineCurve PolesCount=3 KnotsCount=2 Degree=2 IsPeriodic=0
    g193: GeomPoint X=58.0728 Y=-40.8935 Z=0
    g194: GeomPoint X=61.5791 Y=-42.9683 Z=0
    g195: LineSegment StartX=61.5791 StartY=-42.9683 StartZ=0 EndX=165.871 EndY=14.2954 EndZ=0
    g196: LineSegment StartX=165.871 StartY=18.1458 StartZ=0 EndX=61.5791 EndY=75.4095 EndZ=0
    g197: LineSegment StartX=58.0728 StartY=73.3346 StartZ=0 EndX=58.0728 EndY=-40.8935 EndZ=0
    g198: Circle CenterX=302.567 CenterY=-42.9683 CenterZ=0 NormalX=0 NormalY=0 NormalZ=1 AngleXU=0 Radius=1
    g199: Circle CenterX=306.073 CenterY=-44.8935 CenterZ=0 NormalX=0 NormalY=0 NormalZ=1 AngleXU=0 Radius=1
    g200: Circle CenterX=306.073 CenterY=-40.8935 CenterZ=0 NormalX=0 NormalY=0 NormalZ=1 AngleXU=0 Radius=1
    g201: BSplineCurve PolesCount=3 KnotsCount=2 Degree=2 IsPeriodic=0
    g202: GeomPoint X=302.567 Y=-42.9683 Z=0
    g203: GeomPoint X=306.073 Y=-40.8935 Z=0
    g204: Circle CenterX=306.073 CenterY=73.3346 CenterZ=0 NormalX=0 NormalY=0 NormalZ=1 AngleXU=0 Radius=1
    g205: Circle CenterX=306.073 CenterY=77.3346 CenterZ=0 NormalX=0 NormalY=0 NormalZ=1 AngleXU=0 Radius=1
    g206: Circle CenterX=302.567 CenterY=75.4095 CenterZ=0 NormalX=0 NormalY=0 NormalZ=1 AngleXU=0 Radius=1
    g207: BSplineCurve PolesCount=3 KnotsCount=2 Degree=2 IsPeriodic=0
    g208: GeomPoint X=306.073 Y=73.3346 Z=0
    g209: GeomPoint X=302.567 Y=75.4095 Z=0
    g210: LineSegment StartX=302.567 StartY=-42.9683 StartZ=0 EndX=198.275 EndY=14.2954 EndZ=0
    g211: LineSegment StartX=198.275 StartY=18.1458 StartZ=0 EndX=302.567 EndY=75.4095 EndZ=0
    g212: LineSegment StartX=306.073 StartY=73.3346 StartZ=0 EndX=306.073 EndY=-40.8935 EndZ=0
    g213: LineSegment StartX=322.073 StartY=105.865 StartZ=0 EndX=328.643 EndY=105.865 EndZ=0
    g214: LineSegment StartX=318.073 StartY=120.221 StartZ=0 EndX=318.073 EndY=109.865 EndZ=0
    g215: LineSegment StartX=336.157 StartY=107.779 StartZ=0 EndX=362.567 EndY=122.294 EndZ=0
    g216: Circle CenterX=362.073 CenterY=124.221 CenterZ=0 NormalX=0 NormalY=0 NormalZ=1 AngleXU=0 Radius=1
    g217: Circle CenterX=366.073 CenterY=124.221 CenterZ=0 NormalX=0 NormalY=0 NormalZ=1 AngleXU=0 Radius=1
    g218: Circle CenterX=362.567 CenterY=122.294 CenterZ=0 NormalX=0 NormalY=0 NormalZ=1 AngleXU=0 Radius=1
    g219: BSplineCurve PolesCount=3 KnotsCount=2 Degree=2 IsPeriodic=0
    g220: GeomPoint X=362.073 Y=124.221 Z=0
    g221: GeomPoint X=362.567 Y=122.294 Z=0
    g222: Circle CenterX=322.073 CenterY=124.221 CenterZ=0 NormalX=0 NormalY=0 NormalZ=1 AngleXU=0 Radius=1
    g223: Circle CenterX=318.073 CenterY=124.221 CenterZ=0 NormalX=0 NormalY=0 NormalZ=1 AngleXU=0 Radius=1
    g224: Circle CenterX=318.073 CenterY=120.221 CenterZ=0 NormalX=0 NormalY=0 NormalZ=1 AngleXU=0 Radius=1
    g225: BSplineCurve PolesCount=3 KnotsCount=2 Degree=2 IsPeriodic=0
    g226: GeomPoint X=322.073 Y=124.221 Z=0
    g227: GeomPoint X=318.073 Y=120.221 Z=0
    g228: Circle CenterX=322.073 CenterY=105.865 CenterZ=0 NormalX=0 NormalY=0 NormalZ=1 AngleXU=0 Radius=1
    g229: Circle CenterX=318.073 CenterY=105.865 CenterZ=0 NormalX=0 NormalY=0 NormalZ=1 AngleXU=0 Radius=1
    g230: Circle CenterX=318.073 CenterY=109.865 CenterZ=0 NormalX=0 NormalY=0 NormalZ=1 AngleXU=0 Radius=1
    g231: BSplineCurve PolesCount=3 KnotsCount=2 Degree=2 IsPeriodic=0
    g232: GeomPoint X=322.073 Y=105.865 Z=0
    g233: GeomPoint X=318.073 Y=109.865 Z=0
    g234: Circle CenterX=336.157 CenterY=107.779 CenterZ=0 NormalX=0 NormalY=0 NormalZ=1 AngleXU=0 Radius=1
    g235: Circle CenterX=332.651 CenterY=105.853 CenterZ=0 NormalX=0 NormalY=0 NormalZ=1 AngleXU=0 Radius=1
    g236: Circle CenterX=328.643 CenterY=105.865 CenterZ=0 NormalX=0 NormalY=0 NormalZ=1 AngleXU=0 Radius=1
    g237: BSplineCurve PolesCount=3 KnotsCount=2 Degree=2 IsPeriodic=0
    g238: GeomPoint X=336.157 Y=107.779 Z=0
    g239: GeomPoint X=328.643 Y=105.865 Z=0
    g240: LineSegment StartX=322.073 StartY=124.221 StartZ=0 EndX=362.073 EndY=124.221 EndZ=0
    g241: Circle CenterX=371.567 CenterY=-80.8644 CenterZ=0 NormalX=0 NormalY=0 NormalZ=1 AngleXU=0 Radius=1
    g242: Circle CenterX=375.073 CenterY=-82.7896 CenterZ=0 NormalX=0 NormalY=0 NormalZ=1 AngleXU=0 Radius=1
    g243: Circle CenterX=375.073 CenterY=-78.7896 CenterZ=0 NormalX=0 NormalY=0 NormalZ=1 AngleXU=0 Radius=1
    g244: BSplineCurve PolesCount=3 KnotsCount=2 Degree=2 IsPeriodic=0
    g245: GeomPoint X=371.567 Y=-80.8644 Z=0
    g246: GeomPoint X=375.073 Y=-78.7896 Z=0
    g247: Circle CenterX=321.579 CenterY=-53.4075 CenterZ=0 NormalX=0 NormalY=0 NormalZ=1 AngleXU=0 Radius=1
    g248: Circle CenterX=318.073 CenterY=-51.4823 CenterZ=0 NormalX=0 NormalY=0 NormalZ=1 AngleXU=0 Radius=1
    g249: Circle CenterX=318.073 CenterY=-47.4805 CenterZ=0 NormalX=0 NormalY=0 NormalZ=1 AngleXU=0 Radius=1
    g250: BSplineCurve PolesCount=3 KnotsCount=2 Degree=2 IsPeriodic=0
    g251: GeomPoint X=321.579 Y=-53.4075 Z=0
    g252: GeomPoint X=318.073 Y=-47.4805 Z=0
    g253: LineSegment StartX=371.567 StartY=-80.8644 StartZ=0 EndX=321.579 EndY=-53.4075 EndZ=0
    g254: Circle CenterX=321.579 CenterY=-67.3492 CenterZ=0 NormalX=0 NormalY=0 NormalZ=1 AngleXU=0 Radius=1
    g255: Circle CenterX=318.073 CenterY=-65.424 CenterZ=0 NormalX=0 NormalY=0 NormalZ=1 AngleXU=0 Radius=1
    g256: Circle CenterX=318.073 CenterY=-69.424 CenterZ=0 NormalX=0 NormalY=0 NormalZ=1 AngleXU=0 Radius=1
    g257: BSplineCurve PolesCount=3 KnotsCount=2 Degree=2 IsPeriodic=0
    g258: GeomPoint X=321.579 Y=-67.3492 Z=0
    g259: GeomPoint X=318.073 Y=-69.424 Z=0
    g260: Circle CenterX=362.567 CenterY=-89.8542 CenterZ=0 NormalX=0 NormalY=0 NormalZ=1 AngleXU=0 Radius=1
    g261: Circle CenterX=366.073 CenterY=-91.7794 CenterZ=0 NormalX=0 NormalY=0 NormalZ=1 AngleXU=0 Radius=1
    g262: Circle CenterX=362.073 CenterY=-91.7794 CenterZ=0 NormalX=0 NormalY=0 NormalZ=1 AngleXU=0 Radius=1
    g263: BSplineCurve PolesCount=3 KnotsCount=2 Degree=2 IsPeriodic=0
    g264: GeomPoint X=362.567 Y=-89.8542 Z=0
    g265: GeomPoint X=362.073 Y=-91.7794 Z=0
    g266: Circle CenterX=322.073 CenterY=-91.7794 CenterZ=0 NormalX=0 NormalY=0 NormalZ=1 AngleXU=0 Radius=1
    g267: Circle CenterX=318.073 CenterY=-91.7794 CenterZ=0 NormalX=0 NormalY=0 NormalZ=1 AngleXU=0 Radius=1
    g268: Circle CenterX=318.073 CenterY=-87.7794 CenterZ=0 NormalX=0 NormalY=0 NormalZ=1 AngleXU=0 Radius=1
    g269: BSplineCurve PolesCount=3 KnotsCount=2 Degree=2 IsPeriodic=0
    g270: GeomPoint X=322.073 Y=-91.7794 Z=0
    g271: GeomPoint X=318.073 Y=-87.7794 Z=0
    g272: LineSegment StartX=362.567 StartY=-89.8542 StartZ=0 EndX=321.579 EndY=-67.3492 EndZ=0
    g273: LineSegment StartX=318.073 StartY=-69.424 StartZ=0 EndX=318.073 EndY=-87.7794 EndZ=0
    g274: LineSegment StartX=322.073 StartY=-91.7794 StartZ=0 EndX=362.073 EndY=-91.7794 EndZ=0
    g275: Circle CenterX=2.07281 CenterY=124.221 CenterZ=0 NormalX=0 NormalY=0 NormalZ=1 AngleXU=0 Radius=1
    g276: Circle CenterX=1.57905 CenterY=122.295 CenterZ=0 NormalX=0 NormalY=0 NormalZ=1 AngleXU=0 Radius=1
    g277: BSplineCurve PolesCount=3 KnotsCount=2 Degree=2 IsPeriodic=0
    g278: GeomPoint X=2.07281 Y=124.221 Z=0
    g279: GeomPoint X=1.57905 Y=122.295 Z=0
    g280: Circle CenterX=42.0728 CenterY=124.221 CenterZ=0 NormalX=0 NormalY=0 NormalZ=1 AngleXU=0 Radius=1
    g281: Circle CenterX=46.0728 CenterY=124.221 CenterZ=0 NormalX=0 NormalY=0 NormalZ=1 AngleXU=0 Radius=1
    g282: Circle CenterX=46.0728 CenterY=120.221 CenterZ=0 NormalX=0 NormalY=0 NormalZ=1 AngleXU=0 Radius=1
    g283: BSplineCurve PolesCount=3 KnotsCount=2 Degree=2 IsPeriodic=0
    g284: GeomPoint X=42.0728 Y=124.221 Z=0
    g285: GeomPoint X=46.0728 Y=120.221 Z=0
    g286: Circle CenterX=46.0728 CenterY=109.865 CenterZ=0 NormalX=0 NormalY=0 NormalZ=1 AngleXU=0 Radius=1
    g287: Circle CenterX=46.0728 CenterY=105.865 CenterZ=0 NormalX=0 NormalY=0 NormalZ=1 AngleXU=0 Radius=1
    g288: Circle CenterX=42.0728 CenterY=105.865 CenterZ=0 NormalX=0 NormalY=0 NormalZ=1 AngleXU=0 Radius=1
    g289: BSplineCurve PolesCount=3 KnotsCount=2 Degree=2 IsPeriodic=0
    g290: GeomPoint X=46.0728 Y=109.865 Z=0
    g291: GeomPoint X=42.0728 Y=105.865 Z=0
    g292: Circle CenterX=35.5028 CenterY=105.865 CenterZ=0 NormalX=0 NormalY=0 NormalZ=1 AngleXU=0 Radius=1
    g293: Circle CenterX=31.5028 CenterY=105.865 CenterZ=0 NormalX=0 NormalY=0 NormalZ=1 AngleXU=0 Radius=1
    g294: Circle CenterX=27.9965 CenterY=107.79 CenterZ=0 NormalX=0 NormalY=0 NormalZ=1 AngleXU=0 Radius=1
    g295: BSplineCurve PolesCount=3 KnotsCount=2 Degree=2 IsPeriodic=0
    g296: GeomPoint X=35.5028 Y=105.865 Z=0
    g297: GeomPoint X=27.9965 Y=107.79 Z=0
    g298: LineSegment StartX=2.07281 StartY=124.221 StartZ=0 EndX=42.0728 EndY=124.221 EndZ=0
    g299: LineSegment StartX=46.0728 StartY=120.221 StartZ=0 EndX=46.0728 EndY=109.865 EndZ=0
    g300: LineSegment StartX=42.0728 StartY=105.865 StartZ=0 EndX=35.5028 EndY=105.865 EndZ=0
    g301: LineSegment StartX=27.9965 StartY=107.79 StartZ=0 EndX=1.57905 EndY=122.295 EndZ=0
    g302: Circle CenterX=42.5666 CenterY=-67.3492 CenterZ=0 NormalX=0 NormalY=0 NormalZ=1 AngleXU=0 Radius=1
    g303: Circle CenterX=46.0728 CenterY=-65.424 CenterZ=0 NormalX=0 NormalY=0 NormalZ=1 AngleXU=0 Radius=1
    g304: Circle CenterX=46.0728 CenterY=-69.424 CenterZ=0 NormalX=0 NormalY=0 NormalZ=1 AngleXU=0 Radius=1
    g305: BSplineCurve PolesCount=3 KnotsCount=2 Degree=2 IsPeriodic=0
    g306: GeomPoint X=42.5666 Y=-67.3492 Z=0
    g307: GeomPoint X=46.0728 Y=-69.424 Z=0
    g308: Circle CenterX=46.0728 CenterY=-87.7794 CenterZ=0 NormalX=0 NormalY=0 NormalZ=1 AngleXU=0 Radius=1
    g309: Circle CenterX=46.0728 CenterY=-91.7794 CenterZ=0 NormalX=0 NormalY=0 NormalZ=1 AngleXU=0 Radius=1
    g310: Circle CenterX=42.0728 CenterY=-91.7794 CenterZ=0 NormalX=0 NormalY=0 NormalZ=1 AngleXU=0 Radius=1
    g311: BSplineCurve PolesCount=3 KnotsCount=2 Degree=2 IsPeriodic=0
    g312: GeomPoint X=46.0728 Y=-87.7794 Z=0
    g313: GeomPoint X=42.0728 Y=-91.7794 Z=0
    g314: Circle CenterX=2.07281 CenterY=-91.7794 CenterZ=0 NormalX=0 NormalY=0 NormalZ=1 AngleXU=0 Radius=1
    g315: Circle CenterX=-1.92719 CenterY=-91.7794 CenterZ=0 NormalX=0 NormalY=0 NormalZ=1 AngleXU=0 Radius=1
    g316: Circle CenterX=1.57905 CenterY=-89.8542 CenterZ=0 NormalX=0 NormalY=0 NormalZ=1 AngleXU=0 Radius=1
    g317: BSplineCurve PolesCount=3 KnotsCount=2 Degree=2 IsPeriodic=0
    g318: GeomPoint X=2.07281 Y=-91.7794 Z=0
    g319: GeomPoint X=1.57905 Y=-89.8542 Z=0
    g320: LineSegment StartX=2.07281 StartY=-91.7794 StartZ=0 EndX=42.0728 EndY=-91.7794 EndZ=0
    g321: LineSegment StartX=46.0728 StartY=-87.7794 StartZ=0 EndX=46.0728 EndY=-69.424 EndZ=0
    g322: LineSegment StartX=42.5666 StartY=-67.3492 StartZ=0 EndX=1.57905 EndY=-89.8542 EndZ=0
    g323: Circle CenterX=322.073 CenterY=76.4095 CenterZ=0 NormalX=0 NormalY=0 NormalZ=1 AngleXU=0 Radius=4
    g324: BSplineCurve PolesCount=3 KnotsCount=2 Degree=2 IsPeriodic=0
    g325: GeomPoint X=318.073 Y=72.4095 Z=0
    g326: GeomPoint X=322.073 Y=76.4095 Z=0
    g327: Circle CenterX=375.073 CenterY=72.4095 CenterZ=0 NormalX=0 NormalY=0 NormalZ=1 AngleXU=0 Radius=1
    g328: Circle CenterX=375.073 CenterY=76.4095 CenterZ=0 NormalX=0 NormalY=0 NormalZ=1 AngleXU=0 Radius=1
    g329: Circle CenterX=371.073 CenterY=76.4095 CenterZ=0 NormalX=0 NormalY=0 NormalZ=1 AngleXU=0 Radius=1
    g330: BSplineCurve PolesCount=3 KnotsCount=2 Degree=2 IsPeriodic=0
    g331: GeomPoint X=375.073 Y=72.4095 Z=0
    g332: GeomPoint X=371.073 Y=76.4095 Z=0
    g333: LineSegment StartX=322.073 StartY=76.4095 StartZ=0 EndX=371.073 EndY=76.4095 EndZ=0
    g334: LineSegment StartX=318.073 StartY=72.4095 StartZ=0 EndX=318.073 EndY=-47.4805 EndZ=0
    g335: LineSegment StartX=375.073 StartY=72.4095 StartZ=0 EndX=375.073 EndY=-78.7896 EndZ=0
    g336: ArcOfCircle CenterX=-26.9272 CenterY=22.1087 CenterZ=0 NormalX=0 NormalY=0 NormalZ=1 AngleXU=0 Radius=4 StartAngle=5e-16 EndAngle=3.14159
    g337: LineSegment StartX=-22.9272 StartY=22.1087 StartZ=0 EndX=-18.9272 EndY=-83.7794 EndZ=0
    g338: LineSegment StartX=-34.9272 StartY=-83.7794 StartZ=0 EndX=-30.9272 EndY=22.1087 EndZ=0
    g339: ArcOfCircle CenterX=391.073 CenterY=22.1087 CenterZ=0 NormalX=0 NormalY=0 NormalZ=1 AngleXU=0 Radius=4 StartAngle=0 EndAngle=3.14159
    g340: LineSegment StartX=387.073 StartY=22.1087 StartZ=0 EndX=383.073 EndY=-83.7794 EndZ=0
    g341: LineSegment StartX=395.073 StartY=22.1087 StartZ=0 EndX=399.073 EndY=-83.7794 EndZ=0
    g342: Circle CenterX=-10.9272 CenterY=-78.7794 CenterZ=0 NormalX=0 NormalY=0 NormalZ=1 AngleXU=0 Radius=1
    g343: Circle CenterX=-10.9272 CenterY=-82.7794 CenterZ=0 NormalX=0 NormalY=0 NormalZ=1 AngleXU=0 Radius=1
    g344: Circle CenterX=-7.42095 CenterY=-80.8542 CenterZ=0 NormalX=0 NormalY=0 NormalZ=1 AngleXU=0 Radius=1
    g345: BSplineCurve PolesCount=3 KnotsCount=2 Degree=2 IsPeriodic=0
    g346: GeomPoint X=-10.9272 Y=-78.7794 Z=0
    g347: GeomPoint X=-7.42095 Y=-80.8542 Z=0
    g348: Circle CenterX=42.5666 CenterY=-53.4075 CenterZ=0 NormalX=0 NormalY=0 NormalZ=1 AngleXU=0 Radius=1
    g349: Circle CenterX=46.0728 CenterY=-51.4823 CenterZ=0 NormalX=0 NormalY=0 NormalZ=1 AngleXU=0 Radius=1
    g350: Circle CenterX=46.0728 CenterY=-47.4823 CenterZ=0 NormalX=0 NormalY=0 NormalZ=1 AngleXU=0 Radius=1
    g351: BSplineCurve PolesCount=3 KnotsCount=2 Degree=2 IsPeriodic=0
    g352: GeomPoint X=42.5666 Y=-53.4075 Z=0
    g353: GeomPoint X=46.0728 Y=-47.4823 Z=0
    g354: Circle CenterX=46.0728 CenterY=72.4095 CenterZ=0 NormalX=0 NormalY=0 NormalZ=1 AngleXU=0 Radius=1
    g355: Circle CenterX=46.0728 CenterY=76.4095 CenterZ=0 NormalX=0 NormalY=0 NormalZ=1 AngleXU=0 Radius=1
    g356: Circle CenterX=42.0728 CenterY=76.4095 CenterZ=0 NormalX=0 NormalY=0 NormalZ=1 AngleXU=0 Radius=1
    g357: BSplineCurve PolesCount=3 KnotsCount=2 Degree=2 IsPeriodic=0
    g358: GeomPoint X=46.0728 Y=72.4095 Z=0
    g359: GeomPoint X=42.0728 Y=76.4095 Z=0
    g360: Circle CenterX=-6.92718 CenterY=76.4095 CenterZ=0 NormalX=0 NormalY=0 NormalZ=1 AngleXU=0 Radius=1
    g361: Circle CenterX=-10.9272 CenterY=76.4095 CenterZ=0 NormalX=0 NormalY=0 NormalZ=1 AngleXU=0 Radius=1
    g362: Circle CenterX=-10.9272 CenterY=72.4095 CenterZ=0 NormalX=0 NormalY=0 NormalZ=1 AngleXU=0 Radius=1
    g363: BSplineCurve PolesCount=3 KnotsCount=2 Degree=2 IsPeriodic=0
    g364: GeomPoint X=-6.92718 Y=76.4095 Z=0
    g365: GeomPoint X=-10.9272 Y=72.4095 Z=0
    g366: LineSegment StartX=-10.9272 StartY=72.4095 StartZ=0 EndX=-10.9272 EndY=-78.7794 EndZ=0
    g367: LineSegment StartX=-7.42095 StartY=-80.8542 StartZ=0 EndX=42.5666 EndY=-53.4075 EndZ=0
    g368: LineSegment StartX=46.0728 StartY=-47.4823 StartZ=0 EndX=46.0728 EndY=72.4095 EndZ=0
    g369: LineSegment StartX=42.0728 StartY=76.4095 StartZ=0 EndX=-6.92719 EndY=76.4095 EndZ=0
    g370: LineSegment StartX=119.072 StartY=136.221 StartZ=0 EndX=119.072 EndY=-116.228 EndZ=0
    g371: LineSegment StartX=-42.9272 StartY=136.221 StartZ=0 EndX=407.073 EndY=136.221 EndZ=0
    g372: LineSegment StartX=232.072 StartY=136.221 StartZ=0 EndX=220.072 EndY=136.221 EndZ=0
    g373: LineSegment StartX=232.072 StartY=136.221 StartZ=0 EndX=232.072 EndY=124.221 EndZ=0
    g374: LineSegment StartX=220.072 StartY=136.221 StartZ=0 EndX=220.072 EndY=124.221 EndZ=0
    g375: LineSegment StartX=220.072 StartY=136.221 StartZ=0 EndX=226.072 EndY=136.221 EndZ=0
    g376: LineSegment StartX=220.072 StartY=136.221 StartZ=0 EndX=220.072 EndY=130.221 EndZ=0
    g377: LineSegment StartX=220.072 StartY=124.221 StartZ=0 EndX=226.072 EndY=124.221 EndZ=0
    g378: LineSegment StartX=232.072 StartY=124.221 StartZ=0 EndX=232.072 EndY=127.221 EndZ=0
    g379: LineSegment StartX=232.072 StartY=136.221 StartZ=0 EndX=232.072 EndY=133.221 EndZ=0
    g380-g384: Circle x5 (B-spline internal-alignment scaffolding for g385; pole/knot coordinates omitted)
    g385: BSplineCurve PolesCount=5 KnotsCount=3 Degree=3 IsPeriodic=0
    g386: GeomPoint X=232.072 Y=133.221 Z=0
    g387: GeomPoint X=223.072 Y=130.221 Z=0
    g388: GeomPoint X=232.072 Y=127.221 Z=0
    g389: LineSegment StartX=189.124 StartY=124.221 StartZ=0 EndX=302.073 EndY=124.221 EndZ=0
    g390: LineSegment StartX=132.072 StartY=136.221 StartZ=0 EndX=132.072 EndY=124.221 EndZ=0
    g391: LineSegment StartX=132.072 StartY=136.221 StartZ=0 EndX=144.072 EndY=136.221 EndZ=0
    g392: LineSegment StartX=144.072 StartY=136.221 StartZ=0 EndX=144.072 EndY=124.221 EndZ=0
    g393: LineSegment StartX=144.072 StartY=136.221 StartZ=0 EndX=138.072 EndY=136.221 EndZ=0
    g394: LineSegment StartX=144.072 StartY=136.221 StartZ=0 EndX=144.072 EndY=130.221 EndZ=0
    g395: LineSegment StartX=132.072 StartY=136.221 StartZ=0 EndX=132.072 EndY=133.221 EndZ=0
    g396: LineSegment StartX=132.072 StartY=133.221 StartZ=0 EndX=132.072 EndY=127.221 EndZ=0
    g397-g401: Circle x5 (B-spline internal-alignment scaffolding for g402; pole/knot coordinates omitted)
    g402: BSplineCurve PolesCount=5 KnotsCount=3 Degree=3 IsPeriodic=0
    g403: GeomPoint X=132.072 Y=133.221 Z=0
    g404: GeomPoint X=141.072 Y=130.221 Z=0
    g405: GeomPoint X=132.072 Y=127.221 Z=0
    g406: LineSegment StartX=132.072 StartY=124.221 StartZ=0 EndX=175.022 EndY=124.221 EndZ=0
    g407: LineSegment StartX=62.0728 StartY=124.221 StartZ=0 EndX=132.072 EndY=124.221 EndZ=0
    ... +15 more geometry lines
  constraints (718):
    c: Vertical(g0)
    c: Vertical(g1)
    c: Block(g1)
    c: Block(g0)
    c: Weight(g4) = 1
    c: Equal(g4,g5)
    c: Equal(g4,g6)
    c: InternalAlignment(g4,g7)
    c: InternalAlignment(g5,g7)
    c: InternalAlignment(g6,g7)
    c: InternalAlignment(g8,g7)
    c: InternalAlignment(g9,g7)
    c: Weight(g10) = 1
    c: Equal(g10,g11)
    c: Equal(g10,g12)
    c: InternalAlignment(g10,g13)
    c: InternalAlignment(g11,g13)
    c: InternalAlignment(g12,g13)
    c: InternalAlignment(g14,g13)
    c: InternalAlignment(g15,g13)
    c: Block(g13)
    c: Block(g7)
    c: Weight(g16) = 1
    c: Equal(g16,g17)
    c: Equal(g16,g18)
    c: InternalAlignment(g16,g19)
    c: InternalAlignment(g17,g19)
    c: InternalAlignment(g18,g19)
    c: InternalAlignment(g20,g19)
    c: InternalAlignment(g21,g19)
    c: Weight(g22) = 1
    c: Equal(g22,g23)
    c: Equal(g22,g24)
    c: InternalAlignment(g22,g25)
    c: InternalAlignment(g23,g25)
    c: InternalAlignment(g24,g25)
    c: InternalAlignment(g26,g25)
    c: InternalAlignment(g27,g25)
    c: Block(g25)
    c: Block(g19)
    c: Weight(g28) = 1
    c: Equal(g28,g29)
    c: Equal(g28,g30)
    c: InternalAlignment(g28,g31)
    c: InternalAlignment(g29,g31)
    c: InternalAlignment(g30,g31)
    c: InternalAlignment(g32,g31)
    c: InternalAlignment(g33,g31)
    c: Weight(g34) = 1
    c: Equal(g34,g35)
    c: Equal(g34,g36)
    c: InternalAlignment(g34,g37)
    c: InternalAlignment(g35,g37)
    c: InternalAlignment(g36,g37)
    c: InternalAlignment(g38,g37)
    c: InternalAlignment(g39,g37)
    c: Block(g31)
    c: Block(g37)
    c: Coincident(g40,g1)
    c: Coincident(g40,g0)
    c: Horizontal(g40)
    c: Distance(g40) = 450
    c: Weight(g41) = 1
    c: Equal(g41,g42)
    c: Equal(g41,g43)
    c: InternalAlignment(g41,g44)
    c: InternalAlignment(g42,g44)
    c: InternalAlignment(g43,g44)
    c: InternalAlignment(g45,g44)
    c: InternalAlignment(g46,g44)
    c: Block(g44)
    c: Weight(g47) = 1
    c: Equal(g47,g48)
    c: Equal(g47,g49)
    c: InternalAlignment(g47,g50)
    c: InternalAlignment(g48,g50)
    c: InternalAlignment(g49,g50)
    c: InternalAlignment(g51,g50)
    c: InternalAlignment(g52,g50)
    c: Block(g50)
    c: Weight(g53) = 1
    c: Equal(g53,g54)
    c: Equal(g53,g55)
    c: InternalAlignment(g53,g56)
    c: InternalAlignment(g54,g56)
    c: InternalAlignment(g55,g56)
    c: InternalAlignment(g57,g56)
    c: InternalAlignment(g58,g56)
    c: Block(g56)
    c: Weight(g59) = 1
    c: Equal(g59,g60)
    c: Equal(g59,g61)
    c: InternalAlignment(g59,g62)
    c: InternalAlignment(g60,g62)
    c: InternalAlignment(g61,g62)
    c: InternalAlignment(g63,g62)
    c: InternalAlignment(g64,g62)
    c: Block(g62)
    c: Weight(g65) = 1
    c: Equal(g65,g66)
    c: Equal(g65,g67)
    c: InternalAlignment(g65,g68)
    c: InternalAlignment(g66,g68)
    c: InternalAlignment(g67,g68)
    c: InternalAlignment(g69,g68)
    c: InternalAlignment(g70,g68)
    c: Weight(g71) = 1
    c: Equal(g71,g72)
    c: Equal(g71,g73)
    c: InternalAlignment(g71,g74)
    c: InternalAlignment(g72,g74)
    c: InternalAlignment(g73,g74)
    c: InternalAlignment(g75,g74)
    c: InternalAlignment(g76,g74)
    c: Block(g68)
    c: Block(g74)
    c: Coincident(g77,g68)
    c: Coincident(g77,g74)
    c: Vertical(g77)
    c: Coincident(g78,g68)
    c: Coincident(g78,g50)
    c: Coincident(g79,g50)
    c: Coincident(g79,g74)
    c: Weight(g80) = 1
    c: Equal(g80,g81)
    c: Equal(g80,g82)
    c: InternalAlignment(g80,g83)
    c: InternalAlignment(g81,g83)
    c: InternalAlignment(g82,g83)
    c: InternalAlignment(g84,g83)
    c: InternalAlignment(g85,g83)
    c: Weight(g86) = 1
    c: Equal(g86,g87)
    c: Equal(g86,g88)
    c: InternalAlignment(g86,g89)
    c: InternalAlignment(g87,g89)
    c: InternalAlignment(g88,g89)
    c: InternalAlignment(g90,g89)
    c: InternalAlignment(g91,g89)
    c: Block(g83)
    c: Block(g89)
    c: Coincident(g92,g83)
    c: Coincident(g92,g89)
    c: Vertical(g92)
    c: Coincident(g93,g83)
    c: Coincident(g93,g44)
    c: Coincident(g94,g44)
    c: Coincident(g94,g89)
    c: Weight(g95) = 1
    c: Equal(g95,g96)
    c: Equal(g95,g97)
    c: InternalAlignment(g95,g98)
    c: InternalAlignment(g96,g98)
    c: InternalAlignment(g97,g98)
    c: InternalAlignment(g99,g98)
    c: InternalAlignment(g100,g98)
    c: Weight(g101) = 1
    c: Equal(g101,g102)
    c: Equal(g101,g103)
    c: InternalAlignment(g101,g104)
    c: InternalAlignment(g102,g104)
    c: InternalAlignment(g103,g104)
    c: InternalAlignment(g105,g104)
    c: InternalAlignment(g106,g104)
    c: Block(g98)
    c: Block(g104)
    c: Coincident(g107,g98)
    c: Coincident(g107,g104)
    c: Vertical(g107)
    c: Coincident(g108,g104)
    c: Coincident(g108,g62)
    c: Coincident(g109,g62)
    c: Coincident(g109,g98)
    c: Weight(g110) = 1
    c: Equal(g110,g111)
    c: Equal(g110,g112)
    c: InternalAlignment(g110,g113)
    c: InternalAlignment(g111,g113)
    c: InternalAlignment(g112,g113)
    c: InternalAlignment(g114,g113)
    c: InternalAlignment(g115,g113)
    c: Weight(g116) = 1
    c: Equal(g116,g117)
    c: Equal(g116,g118)
    c: InternalAlignment(g116,g119)
    c: InternalAlignment(g117,g119)
    c: InternalAlignment(g118,g119)
    c: InternalAlignment(g120,g119)
    c: InternalAlignment(g121,g119)
    c: Block(g113)
    c: Block(g119)
    c: Coincident(g122,g113)
    c: Coincident(g122,g119)
    c: Vertical(g122)
    c: Coincident(g123,g119)
    c: Coincident(g123,g56)
    c: Coincident(g124,g56)
    c: Coincident(g124,g113)
    c: Weight(g125) = 1
    c: Equal(g125,g126)
    c: Equal(g125,g127)
    c: InternalAlignment(g125,g128)
    c: InternalAlignment(g126,g128)
    c: InternalAlignment(g127,g128)
    c: InternalAlignment(g129,g128)
    c: InternalAlignment(g130,g128)
    c: Weight(g131) = 1
    c: Equal(g131,g132)
    c: Equal(g131,g133)
    c: InternalAlignment(g131,g134)
    c: InternalAlignment(g132,g134)
    c: InternalAlignment(g133,g134)
    c: InternalAlignment(g135,g134)
    c: InternalAlignment(g136,g134)
    c: Weight(g137) = 1
    c: Equal(g137,g138)
    c: Equal(g137,g139)
    c: InternalAlignment(g137,g140)
    c: InternalAlignment(g138,g140)
    c: InternalAlignment(g139,g140)
    c: InternalAlignment(g141,g140)
    c: InternalAlignment(g142,g140)
    c: Weight(g143) = 1
    c: Equal(g143,g144)
    c: Equal(g143,g145)
    c: InternalAlignment(g143,g146)
    c: InternalAlignment(g144,g146)
    c: InternalAlignment(g145,g146)
    c: InternalAlignment(g147,g146)
    c: InternalAlignment(g148,g146)
    c: Block(g146)
    c: Block(g140)
    c: Block(g134)
    c: Block(g128)
    c: Coincident(g149,g25)
    c: Coincident(g149,g146)
    c: Coincident(g150,g146)
    c: Coincident(g150,g140)
    c: Horizontal(g150)
    c: Coincident(g151,g140)
    c: Coincident(g151,g25)
    c: Vertical(g151)
    c: Coincident(g152,g19)
    c: Coincident(g152,g134)
    c: Vertical(g152)
    c: Coincident(g153,g134)
    c: Coincident(g153,g128)
    c: Horizontal(g153)
    c: Coincident(g154,g128)
    c: Coincident(g154,g19)
    c: Weight(g155) = 1
    c: Equal(g155,g156)
    c: Equal(g155,g157)
    c: InternalAlignment(g155,g158)
    c: InternalAlignment(g156,g158)
    c: InternalAlignment(g157,g158)
    c: InternalAlignment(g159,g158)
    c: InternalAlignment(g160,g158)
    c: Weight(g161) = 1
    c: Equal(g161,g162)
    c: Equal(g161,g163)
    c: InternalAlignment(g161,g164)
    c: InternalAlignment(g162,g164)
    c: InternalAlignment(g163,g164)
    c: InternalAlignment(g165,g164)
    c: InternalAlignment(g166,g164)
    c: Weight(g167) = 1
    c: Equal(g167,g168)
    c: Equal(g167,g169)
    c: InternalAlignment(g167,g170)
    c: InternalAlignment(g168,g170)
    c: InternalAlignment(g169,g170)
    c: InternalAlignment(g171,g170)
    c: InternalAlignment(g172,g170)
    c: Weight(g173) = 1
    c: Equal(g173,g174)
    c: Equal(g173,g175)
    c: InternalAlignment(g173,g176)
    c: InternalAlignment(g174,g176)
    c: InternalAlignment(g175,g176)
    c: InternalAlignment(g177,g176)
    c: InternalAlignment(g178,g176)
    c: Block(g176)
    c: Block(g170)
    c: Block(g164)
    c: Block(g158)
    c: Coincident(g179,g170)
    c: Coincident(g179,g7)
    c: Vertical(g179)
    c: Coincident(g180,g13)
    c: Coincident(g180,g164)
    c: Vertical(g180)
    c: Coincident(g181,g158)
    c: Coincident(g181,g13)
    c: Coincident(g182,g7)
    c: Weight(g183) = 1
    c: Equal(g183,g184)
    c: Equal(g183,g185)
    c: InternalAlignment(g183,g186)
    c: InternalAlignment(g184,g186)
    c: InternalAlignment(g185,g186)
    c: InternalAlignment(g187,g186)
    c: InternalAlignment(g188,g186)
    c: Weight(g189) = 1
    c: Equal(g189,g190)
    c: Equal(g189,g191)
    c: InternalAlignment(g189,g192)
    c: InternalAlignment(g190,g192)
    c: InternalAlignment(g191,g192)
    c: InternalAlignment(g193,g192)
    c: InternalAlignment(g194,g192)
    c: Block(g192)
    c: Block(g186)
    c: Coincident(g195,g192)
    c: Coincident(g195,g31)
    c: Coincident(g196,g31)
    c: Coincident(g196,g186)
    c: Coincident(g197,g186)
    c: Coincident(g197,g192)
    c: Vertical(g197)
    c: Weight(g198) = 1
    c: Equal(g198,g199)
    c: Equal(g198,g200)
    c: InternalAlignment(g198,g201)
    c: InternalAlignment(g199,g201)
    c: InternalAlignment(g200,g201)
    c: InternalAlignment(g202,g201)
    c: InternalAlignment(g203,g201)
    c: Weight(g204) = 1
    c: Equal(g204,g205)
    c: Equal(g204,g206)
    c: InternalAlignment(g204,g207)
    c: InternalAlignment(g205,g207)
    c: InternalAlignment(g206,g207)
    c: InternalAlignment(g208,g207)
    c: InternalAlignment(g209,g207)
    c: Block(g207)
    c: Block(g201)
    c: Coincident(g210,g201)
    c: Coincident(g210,g37)
    c: Coincident(g211,g37)
    c: Coincident(g211,g207)
    c: Coincident(g212,g207)
    c: Coincident(g212,g201)
    c: Vertical(g212)
    c: Horizontal(g213)
    c: Block(g213)
    c: Vertical(g214)
    c: Block(g214)
    c: Block(g215)
    c: Weight(g216) = 1
    c: Equal(g216,g217)
    c: Equal(g216,g218)
    c: InternalAlignment(g216,g219)
    c: InternalAlignment(g217,g219)
    c: InternalAlignment(g218,g219)
    c: InternalAlignment(g220,g219)
    c: InternalAlignment(g221,g219)
    c: Weight(g222) = 1
    c: Equal(g222,g223)
    c: Equal(g222,g224)
    c: InternalAlignment(g222,g225)
    c: InternalAlignment(g223,g225)
    c: InternalAlignment(g224,g225)
    c: InternalAlignment(g226,g225)
    c: InternalAlignment(g227,g225)
    c: Weight(g228) = 1
    c: Equal(g228,g229)
    c: Equal(g228,g230)
    c: InternalAlignment(g228,g231)
    c: InternalAlignment(g229,g231)
    c: InternalAlignment(g230,g231)
    c: InternalAlignment(g232,g231)
    c: InternalAlignment(g233,g231)
    c: Weight(g234) = 1
    c: Equal(g234,g235)
    c: Equal(g234,g236)
    c: InternalAlignment(g234,g237)
    c: InternalAlignment(g235,g237)
    c: InternalAlignment(g236,g237)
    c: InternalAlignment(g238,g237)
    c: InternalAlignment(g239,g237)
    c: Block(g219)
    c: Block(g225)
    c: Block(g231)
    c: Block(g237)
    c: Coincident(g240,g225)
    c: Coincident(g240,g219)
    c: Horizontal(g240)
    c: Block(g182)
    c: Weight(g241) = 1
    c: Equal(g241,g242)
    c: Equal(g241,g243)
    c: InternalAlignment(g241,g244)
    c: InternalAlignment(g242,g244)
    c: InternalAlignment(g243,g244)
    c: InternalAlignment(g245,g244)
    c: InternalAlignment(g246,g244)
    c: Weight(g247) = 1
    c: Equal(g247,g248)
    c: Equal(g247,g249)
    c: InternalAlignment(g247,g250)
    c: InternalAlignment(g248,g250)
    c: InternalAlignment(g249,g250)
    c: InternalAlignment(g251,g250)
    c: InternalAlignment(g252,g250)
    c: Block(g244)
    c: Block(g250)
    c: Coincident(g253,g244)
    c: Coincident(g253,g250)
    c: Weight(g254) = 1
    c: Equal(g254,g255)
    c: Equal(g254,g256)
    c: InternalAlignment(g254,g257)
    c: InternalAlignment(g255,g257)
    c: InternalAlignment(g256,g257)
    c: InternalAlignment(g258,g257)
    c: InternalAlignment(g259,g257)
    c: Weight(g260) = 1
    c: Equal(g260,g261)
    c: Equal(g260,g262)
    c: InternalAlignment(g260,g263)
    c: InternalAlignment(g261,g263)
    c: InternalAlignment(g262,g263)
    c: InternalAlignment(g264,g263)
    c: InternalAlignment(g265,g263)
    c: Weight(g266) = 1
    c: Equal(g266,g267)
    c: Equal(g266,g268)
    c: InternalAlignment(g266,g269)
    c: InternalAlignment(g267,g269)
    c: InternalAlignment(g268,g269)
    c: InternalAlignment(g270,g269)
    c: InternalAlignment(g271,g269)
    c: Block(g269)
    c: Block(g263)
    c: Block(g257)
    c: Coincident(g272,g263)
    c: Coincident(g272,g257)
    c: Coincident(g273,g257)
    c: Coincident(g273,g269)
    c: Vertical(g273)
    c: Coincident(g274,g269)
    c: Coincident(g274,g263)
    c: Horizontal(g274)
    c: Weight(g275) = 1
    c: Equal(g275,g276)
    c: InternalAlignment(g275,g277)
    c: InternalAlignment(g276,g277)
    c: InternalAlignment(g278,g277)
    c: InternalAlignment(g279,g277)
    c: Weight(g280) = 1
    c: InternalAlignment(g281,g283)
    c: InternalAlignment(g282,g283)
    c: InternalAlignment(g284,g283)
    c: InternalAlignment(g285,g283)
    c: Weight(g286) = 1
    c: Equal(g286,g287)
    c: Equal(g286,g288)
    c: InternalAlignment(g286,g289)
    c: InternalAlignment(g287,g289)
    c: InternalAlignment(g288,g289)
    c: InternalAlignment(g290,g289)
    c: InternalAlignment(g291,g289)
    c: Equal(g292,g293)
    c: Equal(g292,g294)
    c: InternalAlignment(g292,g295)
    c: InternalAlignment(g293,g295)
    c: InternalAlignment(g294,g295)
    c: InternalAlignment(g296,g295)
    c: InternalAlignment(g297,g295)
    c: Block(g283)
    c: Block(g289)
    c: Block(g295)
    c: Block(g277)
    c: Coincident(g298,g277)
    c: Coincident(g298,g283)
    c: Horizontal(g298)
    c: Coincident(g299,g283)
    c: Coincident(g299,g289)
    c: Vertical(g299)
    c: Coincident(g300,g289)
    c: Coincident(g300,g295)
    c: Horizontal(g300)
    c: Coincident(g301,g295)
    c: Coincident(g301,g277)
    c: Weight(g302) = 1
    c: Equal(g302,g303)
    c: Equal(g302,g304)
    c: InternalAlignment(g302,g305)
    c: InternalAlignment(g303,g305)
    c: InternalAlignment(g304,g305)
    c: InternalAlignment(g306,g305)
    c: InternalAlignment(g307,g305)
    c: Weight(g308) = 1
    c: Equal(g308,g309)
    c: Equal(g308,g310)
    c: InternalAlignment(g308,g311)
    c: InternalAlignment(g309,g311)
    c: InternalAlignment(g310,g311)
    c: InternalAlignment(g312,g311)
    c: Weight(g314) = 1
    c: Equal(g314,g315)
    c: Equal(g314,g316)
    c: InternalAlignment(g314,g317)
    c: InternalAlignment(g315,g317)
    c: InternalAlignment(g316,g317)
    c: InternalAlignment(g318,g317)
    c: InternalAlignment(g319,g317)
    c: Block(g317)
    c: Block(g311)
    c: Block(g305)
    c: Coincident(g320,g317)
    c: Coincident(g320,g311)
    c: Horizontal(g320)
    c: Coincident(g321,g311)
    c: Coincident(g321,g305)
    c: Vertical(g321)
    c: Coincident(g322,g305)
    c: Coincident(g322,g317)
    c: InternalAlignment(g323,g324)
    c: InternalAlignment(g325,g324)
    c: InternalAlignment(g326,g324)
    c: Block(g324)
    c: Equal(g327,g328)
    c: Equal(g327,g329)
    c: InternalAlignment(g327,g330)
    c: InternalAlignment(g328,g330)
    c: InternalAlignment(g329,g330)
    c: InternalAlignment(g331,g330)
    c: InternalAlignment(g332,g330)
    c: Block(g330)
    c: Coincident(g333,g324)
    c: Horizontal(g333)
    c: Block(g333)
    c: Coincident(g334,g324)
    c: Coincident(g334,g250)
    c: Vertical(g334)
    c: Coincident(g335,g330)
    c: Coincident(g335,g244)
    c: Vertical(g335)
    c: Block(g336)
    c: Block(g2)
    c: Distance(g334) = 119.89
    c: Coincident(g337,g336)
    c: Coincident(g337,g2)
    c: Coincident(g338,g2)
    c: Coincident(g338,g336)
    c: Block(g3)
    c: Block(g339)
    c: Coincident(g340,g339)
    c: Coincident(g340,g3)
    c: Coincident(g341,g339)
    c: Coincident(g341,g3)
    c: Block(g341)
    c: Block(g340)
    c: Weight(g342) = 1
    c: Equal(g342,g343)
    c: Equal(g342,g344)
    c: InternalAlignment(g342,g345)
    c: InternalAlignment(g343,g345)
    c: InternalAlignment(g344,g345)
    c: InternalAlignment(g346,g345)
    c: InternalAlignment(g347,g345)
    c: Weight(g348) = 1
    c: Equal(g348,g349)
    c: Equal(g348,g350)
    c: InternalAlignment(g348,g351)
    c: InternalAlignment(g349,g351)
    c: InternalAlignment(g350,g351)
    c: InternalAlignment(g352,g351)
    c: InternalAlignment(g353,g351)
    c: Weight(g354) = 1
    c: Equal(g354,g355)
    c: Equal(g354,g356)
    c: InternalAlignment(g354,g357)
    c: InternalAlignment(g355,g357)
    c: InternalAlignment(g356,g357)
    c: InternalAlignment(g358,g357)
    c: InternalAlignment(g359,g357)
    c: Weight(g360) = 1
    c: Equal(g360,g361)
    c: Equal(g360,g362)
    c: InternalAlignment(g360,g363)
    c: InternalAlignment(g361,g363)
    c: InternalAlignment(g362,g363)
    c: InternalAlignment(g364,g363)
    c: InternalAlignment(g365,g363)
    c: Block(g363)
    c: Block(g357)
    c: Block(g351)
    c: Block(g345)
    c: Coincident(g366,g363)
    c: Coincident(g366,g345)
    c: Vertical(g366)
    c: Coincident(g367,g345)
    c: Coincident(g367,g351)
    c: Coincident(g368,g351)
    c: Coincident(g368,g357)
    c: Vertical(g368)
    c: Coincident(g369,g357)
    c: Coincident(g369,g363)
    c: Horizontal(g369)
    c: Vertical(g370)
    c: Coincident(g371,g0)
    c: Coincident(g371,g1)
    c: Horizontal(g371)
    c: Block(g371)
    c: Distance(g371) = 450
    c: Block(g370)
    c: Distance(g0) = 240
    c: Horizontal(g372)
    c: Distance(g372) = 12
    c: Vertical(g373)
    c: Distance(g373) = 12
    c: Coincident(g374,g372)
    c: Vertical(g374)
    c: Horizontal(g375)
    c: Vertical(g376)
    c: Distance(g376) = 6
    c: Coincident(g376,g372)
    c: Coincident(g375,g372)
    c: Block(g374)
    c: Coincident(g377,g374)
    c: Horizontal(g377)
    c: Distance(g377) = 6
    c: Vertical(g378)
    c: Distance(g378) = 3
    c: Vertical(g379)
    c: Distance(g379) = 3
    c: Coincident(g373,g378)
    c: Coincident(g385,g379)
    c: Weight(g380) = 1
    c: Equal(g380,g381)
    c: Coincident(g381,g375)
    c: Equal(g380,g382)
    c: Coincident(g382,g376)
    c: Equal(g380,g383)
    c: Coincident(g383,g377)
    c: Equal(g380,g384)
    c: Coincident(g385,g378)
    c: InternalAlignment(g380-g384 -> g385) x5
    c: InternalAlignment(g386,g385)
    c: InternalAlignment(g387,g385)
    c: InternalAlignment(g388,g385)
    c: Coincident(g389,g164)
    c: Coincident(g389,g158)
    c: Horizontal(g389)
    c: Block(g385)
    c: Vertical(g390)
    c: Distance(g390) = 12
    c: Horizontal(g391)
    c: Distance(g391) = 12
    c: Coincident(g392,g391)
    c: Vertical(g392)
    c: Distance(g392) = 12
    c: Horizontal(g393)
    c: Distance(g393) = 6
    c: Coincident(g393,g391)
    c: Vertical(g394)
    c: Distance(g394) = 6
    c: Coincident(g394,g391)
    c: Vertical(g395)
    c: Distance(g395) = 3
    c: Vertical(g396)
    c: Distance(g396) = 6
    c: Coincident(g396,g395)
    c: Coincident(g402,g395)
    c: Weight(g397) = 1
    c: Equal(g397,g398)
    c: Coincident(g398,g393)
    c: Equal(g397,g399)
    c: Coincident(g399,g394)
    c: Equal(g397,g400)
    c: Equal(g397,g401)
    c: Coincident(g402,g396)
    c: InternalAlignment(g397-g401 -> g402) x5
    c: InternalAlignment(g403,g402)
    c: InternalAlignment(g404,g402)
    c: InternalAlignment(g405,g402)
    c: Coincident(g406,g390)
    c: Coincident(g406,g170)
    c: Horizontal(g406)
    c: Block(g402)
    c: Coincident(g407,g176)
    c: Coincident(g407,g390)
    c: Horizontal(g407)
    c: Block(g406)
    c: Coincident(g409,g390)
    c: PointOnObject(g409,g153)
    c: Vertical(g409)
    c: Block(g410)
    c: Coincident(g411,g410)
    c: Vertical(g411)
    c: PointOnObject(g411,g40)
    c: Block(g411)
    c: Coincident(g412,g410)
    c: Vertical(g412)
    c: Block(g412)
    c: Vertical(g413)
    c: Distance(g413) = 3
    c: Equal(g380,g416) = 1
    c: Equal(g416,g417)
    c: InternalAlignment(g416,g418)
    c: InternalAlignment(g417,g418)
    c: InternalAlignment(g414,g418)
    c: InternalAlignment(g415,g418)
    c: InternalAlignment(g419,g418)
    c: Block(g418)
    c: Coincident(g419,g413)
    c: Coincident(g420,g418)
    c: PointOnObject(g420,g150)
    c: Vertical(g420)
    c: PointOnObject(g421,g211)
    c: Coincident(g422,g421)
    c: Block(g421)
    c: Perpendicular(g422,g211)
    c: PointOnObject(g422,g79)
FEATURE [Part::Extrusion] Extrude005
  Base = -> Sketch003
  Dir = (0,0,1)
  DirMode = 2
  FaceMakerClass = Part::FaceMakerBullseye
  LengthFwd = 24
  LengthRev = 0
  Solid = true
  Symmetric = false
